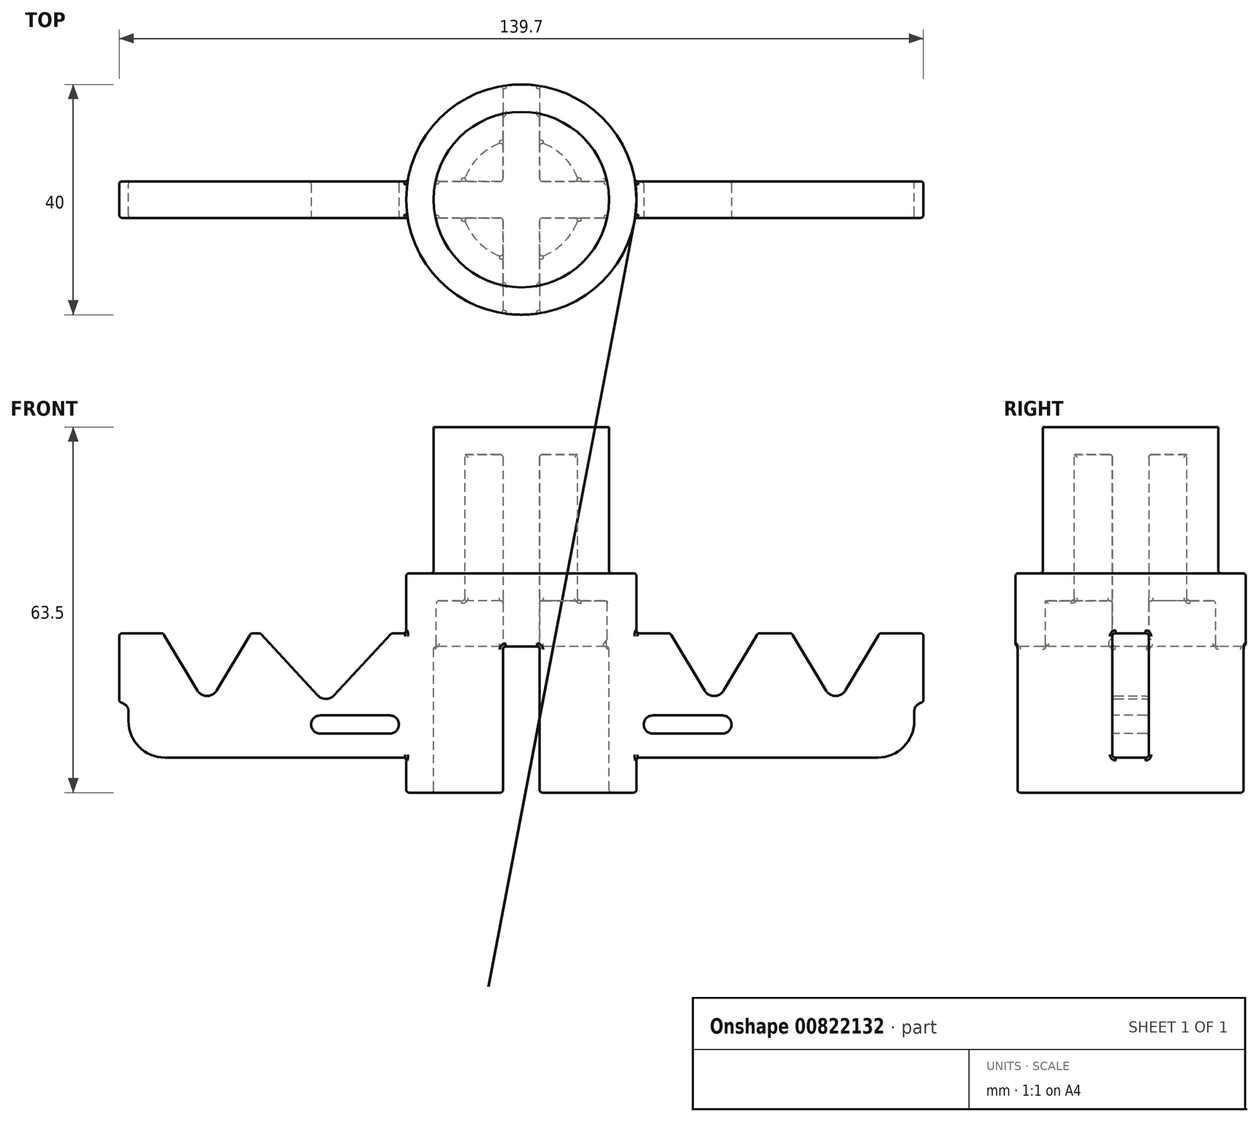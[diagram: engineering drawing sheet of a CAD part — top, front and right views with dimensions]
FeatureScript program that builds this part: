
annotation { "Feature Type Name" : "Feature", "Feature Type Description" : "" }
export const myFeature = defineFeature(function(context is Context, id is Id, definition is map)
    precondition{}
    {
        {
            var Q0;
            Q0=qCreatedBy(makeId("Front.planeOp"),FACE);
            var sketch = newSketch(context, id + "F0", { "sketchPlane" : qUnion([Q0])});
            skLineSegment(sketch, "E0", {"start": v(0, -25.67) * mm, "end": v(61.91, -25.67) * mm});
            skLineSegment(sketch, "E1", {"start": v(69.34, -4.08) * mm, "end": v(62.23, -4.08) * mm});
            skLineSegment(sketch, "E2.trimOffspring", {"start": v(12.23, -4.08) * mm, "end": v(0, -4.08) * mm});
            skLineSegment(sketch, "E3.trimOffspring", {"start": v(47, -4.08) * mm, "end": v(41.1, -4.08) * mm});
            skPoint(sketch, "E4.visualSharp", {"position": v(69.85, -4.08) * mm});
            skArc(sketch, "E4.filletArc", {"start": v(69.85, -4.58) * mm, "mid": v(69.7, -4.22) * mm, "end": v(69.34, -4.08) * mm});
            skPoint(sketch, "E5.visualSharp", {"position": v(69.85, -25.67) * mm});
            skLineSegment(sketch, "E6", {"start": v(0, -46.25) * mm, "end": v(0, -19.99) * mm, "construction": true});
            skLineSegment(sketch, "E7", {"start": v(12.23, -4.08) * mm, "end": v(25.87, -4.08) * mm});
            skLineSegment(sketch, "E8.MirrorCS", {"start": v(0, 38.1) * mm, "end": v(0, 11.84) * mm, "construction": true});
            skArc(sketch, "E9", {"start": v(69.85, -16.1) * mm, "mid": v(68.8, -16.49) * mm, "end": v(68.26, -17.47) * mm});
            skLineSegment(sketch, "E10.trimOffspring", {"start": v(69.85, -16.1) * mm, "end": v(69.85, -4.58) * mm});
            skLineSegment(sketch, "E11", {"start": v(68.26, -17.47) * mm, "end": v(68.26, -19.32) * mm});
            skPoint(sketch, "E12.newPointB", {"position": v(63.5, -25.67) * mm});
            skArc(sketch, "E12.filletArc", {"start": v(61.91, -25.67) * mm, "mid": v(66.4, -23.8) * mm, "end": v(68.26, -19.32) * mm});
            skArc(sketch, "E13.MirrorCS", {"start": v(-69.85, -4.58) * mm, "mid": v(-69.7, -4.22) * mm, "end": v(-69.34, -4.08) * mm});
            skLineSegment(sketch, "E14.MirrorCS", {"start": v(-69.85, -16.1) * mm, "end": v(-69.85, -4.58) * mm});
            skArc(sketch, "E15.MirrorCS", {"start": v(-69.85, -16.1) * mm, "mid": v(-68.8, -16.49) * mm, "end": v(-68.26, -17.47) * mm});
            skLineSegment(sketch, "E16.MirrorCS", {"start": v(-12.23, -4.08) * mm, "end": v(0, -4.08) * mm});
            skLineSegment(sketch, "E17.MirrorCS", {"start": v(-68.26, -17.47) * mm, "end": v(-68.26, -19.32) * mm});
            skLineSegment(sketch, "E18.MirrorCS", {"start": v(-12.23, -4.08) * mm, "end": v(-15.7, -4.08) * mm});
            skLineSegment(sketch, "E19.MirrorCS", {"start": v(-69.34, -4.08) * mm, "end": v(-62.23, -4.08) * mm});
            skLineSegment(sketch, "E20.MirrorCS", {"start": v(0, -25.67) * mm, "end": v(-61.91, -25.67) * mm});
            skPoint(sketch, "E21.MirrorP", {"position": v(-69.85, -4.08) * mm});
            skPoint(sketch, "E22.MirrorP", {"position": v(-69.85, -25.67) * mm});
            skArc(sketch, "E23.MirrorCS", {"start": v(-61.91, -25.67) * mm, "mid": v(-66.4, -23.8) * mm, "end": v(-68.26, -19.32) * mm});
            skPoint(sketch, "E24.MirrorP", {"position": v(-63.5, -25.67) * mm});
            skLineSegment(sketch, "E25", {"start": v(62.23, -4.08) * mm, "end": v(56.24, -14.05) * mm});
            skLineSegment(sketch, "E26", {"start": v(52.98, -14.05) * mm, "end": v(47, -4.08) * mm});
            skLineSegment(sketch, "E27", {"start": v(41.1, -4.08) * mm, "end": v(35.12, -14.05) * mm});
            skLineSegment(sketch, "E28", {"start": v(31.85, -14.05) * mm, "end": v(25.87, -4.08) * mm});
            skLineSegment(sketch, "E29.MirrorCS", {"start": v(-47, -4.08) * mm, "end": v(-45.38, -4.08) * mm});
            skLineSegment(sketch, "E30.MirrorCS", {"start": v(-52.98, -14.05) * mm, "end": v(-47, -4.08) * mm});
            skLineSegment(sketch, "E31.MirrorCS", {"start": v(-62.23, -4.08) * mm, "end": v(-56.24, -14.05) * mm});
            skPoint(sketch, "E32.visualSharp", {"position": v(-54.61, -16.78) * mm});
            skArc(sketch, "E32.filletArc", {"start": v(-56.24, -14.05) * mm, "mid": v(-54.61, -14.98) * mm, "end": v(-52.98, -14.05) * mm});
            skPoint(sketch, "E33.visualSharp", {"position": v(33.49, -16.78) * mm});
            skArc(sketch, "E33.filletArc", {"start": v(31.85, -14.05) * mm, "mid": v(33.49, -14.98) * mm, "end": v(35.12, -14.05) * mm});
            skPoint(sketch, "E34.visualSharp", {"position": v(54.61, -16.78) * mm});
            skArc(sketch, "E34.filletArc", {"start": v(52.98, -14.05) * mm, "mid": v(54.61, -14.98) * mm, "end": v(56.24, -14.05) * mm});
            skPoint(sketch, "E35.endSnap0", {"position": v(-54.61, -14.98) * mm});
            skLineSegment(sketch, "E36", {"start": v(-45.38, -4.08) * mm, "end": v(-35.35, -14.87) * mm});
            skLineSegment(sketch, "E37", {"start": v(-32.56, -14.87) * mm, "end": v(-22.52, -4.08) * mm});
            skLineSegment(sketch, "E38", {"start": v(-15.7, -4.08) * mm, "end": v(-22.52, -4.08) * mm});
            skPoint(sketch, "E39.visualSharp", {"position": v(-33.95, -16.37) * mm});
            skArc(sketch, "E39.filletArc", {"start": v(-35.35, -14.87) * mm, "mid": v(-33.95, -15.48) * mm, "end": v(-32.56, -14.87) * mm});
            skSolve(sketch);
        }
        {
            var Q0;
            Q0 = qSketchRegion(id + "F0", true);
            extrude(context, id + "F1", {"entities" : qUnion([Q0]), "depth" : 3.17 * mm, "offsetDistance" : 25.4 * mm, "hasSecondDirection" : true, "secondDirectionOppositeDirection" : true, "secondDirectionDepth" : 3.17 * mm});
        }
        {
            var Q0;
            Q0=qCreatedBy(makeId("Top.planeOp"),FACE);
            var sketch = newSketch(context, id + "F2", { "sketchPlane" : qUnion([Q0])});
            skCircle(sketch, "E40.0", {"center": v(0, 0) * mm, "radius": 20 * mm});
            skSolve(sketch);
        }
        {
            var Q0;
            Q0=makeQuery(id+"F2.imprint","IMPRINT",FACE,{"disambiguationData":[TD([[makeQuery(id+"F2.imprint","IMPRINT",EDGE,{"derivedFrom":sQuery(id+"F2.wireOp",EDGE,"KXCwf9rt-CnZg-olNI-KTR3-sV1Am3sWeLhQ")}),-1.0]])]});
            var Q1;
            Q1=makeQuery(id+"F2.imprint","IMPRINT",FACE,{"disambiguationData":[TD([[makeQuery(id+"F2.imprint","IMPRINT",EDGE,{"derivedFrom":sQuery(id+"F2.wireOp",EDGE,"E40.0")}),1.0]])]});
            extrude(context, id + "F3", {"entities" : qUnion([Q0, Q1]), "operationType" : NewBodyOperationType.ADD, "oppositeDirection" : true, "depth" : 31.75 * mm, "offsetDistance" : 25.4 * mm, "hasSecondDirection" : true, "secondDirectionOppositeDirection" : false, "secondDirectionDepth" : 31.75 * mm});
        }
        {
            var Q0;
            Q0=makeQuery(id+"F3.opExtrude","CAP_FACE",FACE,{"disambiguationData":[OSD([sQuery(id+"F2.wireOp",EDGE,"E40.0")])],"isStart":false});
            var sketch = newSketch(context, id + "F4", { "sketchPlane" : qUnion([Q0])});
            skCircle(sketch, "E41", {"center": v(0, 0) * mm, "radius": 15.24 * mm});
            skSolve(sketch);
        }
        {
            var Q0;
            Q0=makeQuery(id+"F3.opExtrude","CAP_FACE",FACE,{"disambiguationData":[OSD([sQuery(id+"F2.wireOp",EDGE,"E40.0")])],"isStart":true});
            var sketch = newSketch(context, id + "F5", { "sketchPlane" : qUnion([Q0])});
            skCircle(sketch, "E42", {"center": v(0, 0) * mm, "radius": 15.24 * mm});
            skCircle(sketch, "E43", {"center": v(0, 0) * mm, "radius": 25.4 * mm});
            skSolve(sketch);
        }
        {
            var Q0;
            Q0=makeQuery(id+"F5.imprint","IMPRINT",FACE,{"disambiguationData":[TD([[makeQuery(id+"F5.imprint","IMPRINT",EDGE,{"derivedFrom":sQuery(id+"F5.wireOp",EDGE,"E43")}),1.0]])]});
            var Q1;
            Q1=makeQuery(id+"F5.imprint","IMPRINT",FACE,{"disambiguationData":[TD([[makeQuery(id+"F5.imprint","IMPRINT",EDGE,{"derivedFrom":sQuery(id+"F5.wireOp",EDGE,"E42")}),-1.0]])]});
            extrude(context, id + "F6", {"entities" : qUnion([Q0, Q1]), "operationType" : NewBodyOperationType.REMOVE, "oppositeDirection" : true, "depth" : 25.4 * mm, "offsetDistance" : 25.4 * mm});
        }
        {
            var Q0;
            Q0=makeQuery(id+"F3.opExtrude","CAP_FACE",FACE,{"disambiguationData":[OSD([sQuery(id+"F2.wireOp",EDGE,"E40.0")])],"isStart":false});
            shell(context, id + "F7", {"entities" : qUnion([Q0]), "thickness" : 4.76 * mm});
        }
        {
            var Q0;
            Q0=makeQuery(id+"F4.imprint","IMPRINT",FACE,{"disambiguationData":[TD([[makeQuery(id+"F4.imprint","IMPRINT",EDGE,{"derivedFrom":sQuery(id+"F4.wireOp",EDGE,"E41")}),1.0]])]});
            extrude(context, id + "F8", {"entities" : qUnion([Q0]), "operationType" : NewBodyOperationType.REMOVE, "oppositeDirection" : true, "depth" : 25.4 * mm, "offsetDistance" : 25.4 * mm});
        }
        {
            var Q0;
            Q0=qCreatedBy(makeId("Front.planeOp"),FACE);
            var sketch = newSketch(context, id + "F9", { "sketchPlane" : qUnion([Q0])});
            skLineSegment(sketch, "E44.bottom", {"start": v(3.17, -6.35) * mm, "end": v(-3.18, -6.35) * mm});
            skLineSegment(sketch, "E44.top", {"start": v(3.18, -35.57) * mm, "end": v(-3.17, -35.57) * mm});
            skLineSegment(sketch, "E44.left", {"start": v(3.17, -6.35) * mm, "end": v(3.18, -35.57) * mm});
            skLineSegment(sketch, "E44.right", {"start": v(-3.18, -6.35) * mm, "end": v(-3.17, -35.57) * mm});
            skSolve(sketch);
        }
        {
            var Q0;
            Q0=makeQuery(id+"F9.imprint","IMPRINT",FACE,{"disambiguationData":[TD([[makeQuery(id+"F9.imprint","IMPRINT",EDGE,{"derivedFrom":sQuery(id+"F9.wireOp",EDGE,"E44.bottom")}),1.0]])]});
            extrude(context, id + "F10", {"entities" : qUnion([Q0]), "operationType" : NewBodyOperationType.REMOVE, "endBound" : BoundingType.THROUGH_ALL, "oppositeDirection" : true, "depth" : 25.4 * mm, "offsetDistance" : 25.4 * mm, "hasSecondDirection" : true, "secondDirectionBound" : SecondDirectionBoundingType.THROUGH_ALL, "secondDirectionOppositeDirection" : false, "secondDirectionDepth" : 25.4 * mm});
        }
        {
            var Q0;
            Q0=qCreatedBy(makeId("Top.planeOp"),FACE);
            cPlane(context, id + "F11", {"entities" : qUnion([Q0]), "cplaneType" : CPlaneType.OFFSET, "offset" : 6.35 * mm, "oppositeDirection" : true, "width" : 152.4 * mm, "height" : 152.4 * mm});
        }
        {
            var Q0;
            Q0=qCreatedBy(id+"F11.planeOp",FACE);
            var sketch = newSketch(context, id + "F12", { "sketchPlane" : qUnion([Q0])});
            skLineSegment(sketch, "E45.bottom", {"start": v(18.4, 3.18) * mm, "end": v(-18.44, 3.17) * mm});
            skLineSegment(sketch, "E45.top", {"start": v(18.4, -3.18) * mm, "end": v(-18.44, -3.18) * mm});
            skLineSegment(sketch, "E45.left", {"start": v(18.4, 3.18) * mm, "end": v(18.4, -3.18) * mm});
            skLineSegment(sketch, "E45.right", {"start": v(-18.44, 3.17) * mm, "end": v(-18.44, -3.18) * mm});
            skLineSegment(sketch, "E46.bottom", {"start": v(3.17, 17.5) * mm, "end": v(-3.18, 17.5) * mm});
            skLineSegment(sketch, "E46.top", {"start": v(3.18, -17.88) * mm, "end": v(-3.17, -17.88) * mm});
            skLineSegment(sketch, "E46.left", {"start": v(3.17, 17.5) * mm, "end": v(3.18, -17.88) * mm});
            skLineSegment(sketch, "E46.right", {"start": v(-3.18, 17.5) * mm, "end": v(-3.17, -17.88) * mm});
            skSolve(sketch);
        }
        {
            var Q0;
            {var subQ5=sQuery(id+"F12.wireOp",EDGE,"E46.bottom");Q0=makeQuery(id+"F12.imprint","IMPRINT",FACE,{"disambiguationData":[TD([[makeQuery(id+"F12.imprint","IMPRINT",EDGE,{"derivedFrom":subQ5}),1.0]])]});}
            var Q1;
            {var subQ0=sQuery(id+"F12.wireOp",EDGE,"E45.left");Q1=makeQuery(id+"F12.imprint","IMPRINT",FACE,{"disambiguationData":[TD([[makeQuery(id+"F12.imprint","IMPRINT",EDGE,{"derivedFrom":subQ0}),-1.0]])]});}
            var Q2;
            {var subQ0=sQuery(id+"F12.wireOp",EDGE,"E45.right");Q2=makeQuery(id+"F12.imprint","IMPRINT",FACE,{"disambiguationData":[TD([[makeQuery(id+"F12.imprint","IMPRINT",EDGE,{"derivedFrom":subQ0}),1.0]])]});}
            var Q3;
            {var subQ0=sQuery(id+"F12.wireOp",EDGE,"E46.left");var subQ1=sQuery(id+"F12.wireOp",EDGE,"E45.bottom");var subQ2=makeQuery(id+"F12.imprint","INTERSECT",VERTEX,{"derivedFrom":[subQ1,subQ0]});Q3=makeQuery(id+"F12.imprint","IMPRINT",FACE,{"disambiguationData":[TD([[makeQuery(id+"F12.imprint","IMPRINT",EDGE,{"disambiguationData":[TD([[subQ2,-1.0]])],"derivedFrom":subQ1}),1.0]])]});}
            var Q4;
            {var subQ5=sQuery(id+"F12.wireOp",EDGE,"E46.top");Q4=makeQuery(id+"F12.imprint","IMPRINT",FACE,{"disambiguationData":[TD([[makeQuery(id+"F12.imprint","IMPRINT",EDGE,{"derivedFrom":subQ5}),-1.0]])]});}
            var Q5;
            Q5=makeQuery(id+"F3.opExtrude","CAP_FACE",FACE,{"disambiguationData":[OSD([sQuery(id+"F2.wireOp",EDGE,"E40.0")])],"isStart":true});
            extrude(context, id + "F13", {"entities" : qUnion([Q0, Q1, Q2, Q3, Q4]), "operationType" : NewBodyOperationType.ADD, "endBound" : BoundingType.UP_TO_SURFACE, "depth" : 25.4 * mm, "endBoundEntityFace" : qUnion([Q5]), "offsetDistance" : 25.4 * mm});
        }
        {
            var Q0;
            Q0 = qSketchRegion(id + "F5", true);
            extrude(context, id + "F14", {"entities" : qUnion([Q0]), "operationType" : NewBodyOperationType.REMOVE, "oppositeDirection" : true, "depth" : 25.4 * mm, "offsetDistance" : 25.4 * mm});
        }
        {
            var Q0;
            {var subQ0=sQuery(id+"F0.wireOp",EDGE,"E12.filletArc");var subQ1=sQuery(id+"F0.wireOp",EDGE,"E11");var subQ2=sQuery(id+"F0.wireOp",EDGE,"E10.trimOffspring");var subQ3=sQuery(id+"F0.wireOp",EDGE,"E9");var subQ4=sQuery(id+"F0.wireOp",EDGE,"E25");var subQ5=sQuery(id+"F0.wireOp",EDGE,"E4.filletArc");var subQ6=sQuery(id+"F0.wireOp",EDGE,"E20.MirrorCS");var subQ7=sQuery(id+"F0.wireOp",EDGE,"E0");var subQ8=sQuery(id+"F0.wireOp",EDGE,"E1");var subQ9=sQuery(id+"F0.wireOp",EDGE,"E18.MirrorCS");var subQ10=sQuery(id+"F0.wireOp",EDGE,"E16.MirrorCS");var subQ11=sQuery(id+"F0.wireOp",EDGE,"E7");var subQ12=sQuery(id+"F0.wireOp",EDGE,"E2.trimOffspring");var subQ13=sQuery(id+"F0.wireOp",EDGE,"E3.trimOffspring");var subQ14=sQuery(id+"F0.wireOp",EDGE,"E26");var subQ15=sQuery(id+"F0.wireOp",EDGE,"E27");var subQ16=sQuery(id+"F0.wireOp",EDGE,"E28");Q0=makeQuery(id+"F3.boolean.opBoolean","SPLIT",FACE,{"disambiguationData":[TD([makeQuery(id+"F1.opExtrude","SWEPT_FACE",FACE,{"disambiguationData":[OSD([subQ8])]})])],"derivedFrom":makeQuery(id+"F1.opExtrude","CAP_FACE",FACE,{"disambiguationData":[OSD([subQ7,subQ8,subQ12,subQ13,subQ5,subQ11,subQ3,subQ2,subQ1,subQ0,sQuery(id+"F0.wireOp",EDGE,"E13.MirrorCS"),sQuery(id+"F0.wireOp",EDGE,"E14.MirrorCS"),sQuery(id+"F0.wireOp",EDGE,"E15.MirrorCS"),subQ10,sQuery(id+"F0.wireOp",EDGE,"E17.MirrorCS"),sQuery(id+"F0.wireOp",EDGE,"E19.MirrorCS"),subQ6,sQuery(id+"F0.wireOp",EDGE,"E23.MirrorCS"),subQ4,subQ14,subQ15,subQ16,sQuery(id+"F0.wireOp",EDGE,"E29.MirrorCS"),subQ9,sQuery(id+"F0.wireOp",EDGE,"74dd9322-9861-4298-9e9e-bce7e45bb9e62.MirrorCS"),sQuery(id+"F0.wireOp",EDGE,"74dd9322-9861-4298-9e9e-bce7e45bb9e63.MirrorCS"),sQuery(id+"F0.wireOp",EDGE,"E30.MirrorCS"),sQuery(id+"F0.wireOp",EDGE,"E31.MirrorCS")])],"isStart":false})});}
            var sketch = newSketch(context, id + "F15", { "sketchPlane" : qUnion([Q0])});
            skLineSegment(sketch, "E47.bottom", {"start": v(22.87, -18.34) * mm, "end": v(34.93, -18.34) * mm});
            skLineSegment(sketch, "E47.top", {"start": v(22.87, -21.51) * mm, "end": v(34.93, -21.51) * mm});
            skLineSegment(sketch, "E47.left", {"start": v(21.28, -19.92) * mm, "end": v(21.28, -19.92) * mm});
            skLineSegment(sketch, "E47.right", {"start": v(36.52, -19.92) * mm, "end": v(36.52, -19.92) * mm});
            skPoint(sketch, "E48.visualSharp", {"position": v(21.28, -18.34) * mm});
            skArc(sketch, "E48.filletArc", {"start": v(22.87, -18.34) * mm, "mid": v(21.74, -18.8) * mm, "end": v(21.28, -19.92) * mm});
            skPoint(sketch, "E49.visualSharp", {"position": v(36.52, -18.34) * mm});
            skArc(sketch, "E49.filletArc", {"start": v(36.52, -19.92) * mm, "mid": v(36.05, -18.8) * mm, "end": v(34.93, -18.34) * mm});
            skPoint(sketch, "E50.visualSharp", {"position": v(36.52, -21.51) * mm});
            skArc(sketch, "E50.filletArc", {"start": v(34.93, -21.51) * mm, "mid": v(36.05, -21.05) * mm, "end": v(36.52, -19.92) * mm});
            skPoint(sketch, "E51.visualSharp", {"position": v(21.28, -21.51) * mm});
            skArc(sketch, "E51.filletArc", {"start": v(21.28, -19.92) * mm, "mid": v(21.74, -21.05) * mm, "end": v(22.87, -21.51) * mm});
            skLineSegment(sketch, "E52", {"start": v(0, 0) * mm, "end": v(0, 36.32) * mm, "construction": true});
            skLineSegment(sketch, "E53.MirrorCS", {"start": v(-36.52, -19.92) * mm, "end": v(-36.52, -19.92) * mm});
            skLineSegment(sketch, "E54.MirrorCS", {"start": v(-21.28, -19.92) * mm, "end": v(-21.28, -19.92) * mm});
            skPoint(sketch, "E55.MirrorP", {"position": v(-36.52, -18.34) * mm});
            skPoint(sketch, "E56.MirrorP", {"position": v(-21.28, -21.51) * mm});
            skPoint(sketch, "E57.MirrorP", {"position": v(-21.28, -18.34) * mm});
            skArc(sketch, "E58.MirrorCS", {"start": v(-34.93, -21.51) * mm, "mid": v(-36.05, -21.05) * mm, "end": v(-36.52, -19.92) * mm});
            skArc(sketch, "E59.MirrorCS", {"start": v(-36.52, -19.92) * mm, "mid": v(-36.05, -18.8) * mm, "end": v(-34.93, -18.34) * mm});
            skPoint(sketch, "E60.MirrorP", {"position": v(-36.52, -21.51) * mm});
            skArc(sketch, "E61.MirrorCS", {"start": v(-22.87, -18.34) * mm, "mid": v(-21.74, -18.8) * mm, "end": v(-21.28, -19.92) * mm});
            skArc(sketch, "E62.MirrorCS", {"start": v(-21.28, -19.92) * mm, "mid": v(-21.74, -21.05) * mm, "end": v(-22.87, -21.51) * mm});
            skLineSegment(sketch, "E63", {"start": v(-34.93, -18.34) * mm, "end": v(-22.87, -18.34) * mm});
            skLineSegment(sketch, "E64", {"start": v(-34.93, -21.51) * mm, "end": v(-22.87, -21.51) * mm});
            skSolve(sketch);
        }
        {
            var Q0;
            Q0 = qSketchRegion(id + "F15", true);
            extrude(context, id + "F16", {"entities" : qUnion([Q0]), "operationType" : NewBodyOperationType.REMOVE, "oppositeDirection" : true, "depth" : 25.4 * mm, "offsetDistance" : 25.4 * mm});
        }
        {
            var Q0;
            {var subQ0=sQuery(id+"F2.wireOp",EDGE,"E40.0");Q0=makeQuery(id+"F10.boolean.opBoolean","SPLIT",EDGE,{"disambiguationData":[TD([makeQuery(id+"F10.opExtrude","SWEPT_FACE",FACE,{"disambiguationData":[OSD([sQuery(id+"F9.wireOp",EDGE,"E44.right")])]})])],"derivedFrom":makeQuery(id+"F7.opShell","OFFSET_EDGE",EDGE,{"disambiguationData":[OSD([subQ0])]})});}
            var Q1;
            {var subQ0=sQuery(id+"F12.wireOp",EDGE,"E46.left");Q1=makeQuery(id+"F13.opExtrude","CAP_EDGE",EDGE,{"disambiguationData":[OSD([subQ0]),TDD([makeQuery(id+"F12.imprint","IMPRINT",EDGE,{"disambiguationData":[TD([[makeQuery(id+"F12.imprint","INTERSECT",VERTEX,{"derivedFrom":[sQuery(id+"F12.wireOp",EDGE,"E46.top"),subQ0]}),1.0]])],"derivedFrom":subQ0})])],"isStart":true});}
            var Q2;
            Q2=makeQuery(id+"F10.boolean.opBoolean","INTERSECT",EDGE,{"disambiguationData":[OD(0.0)],"derivedFrom":[makeQuery(id+"F3.opExtrude","SWEPT_FACE",FACE,{"disambiguationData":[OSD([sQuery(id+"F2.wireOp",EDGE,"E40.0")])]}),makeQuery(id+"F10.opExtrude","SWEPT_FACE",FACE,{"disambiguationData":[OSD([sQuery(id+"F9.wireOp",EDGE,"E44.bottom")])]})]});
            var Q3;
            {var subQ0=sQuery(id+"F2.wireOp",EDGE,"E40.0");Q3=makeQuery(id+"F10.boolean.opBoolean","SPLIT",EDGE,{"disambiguationData":[TD([makeQuery(id+"F10.opExtrude","SWEPT_FACE",FACE,{"disambiguationData":[OSD([sQuery(id+"F9.wireOp",EDGE,"E44.left")])]})])],"derivedFrom":makeQuery(id+"F7.opShell","OFFSET_EDGE",EDGE,{"disambiguationData":[OSD([subQ0])]})});}
            var Q4;
            Q4=makeQuery(id+"F10.boolean.opBoolean","INTERSECT",EDGE,{"disambiguationData":[OD(1.0)],"derivedFrom":[makeQuery(id+"F3.opExtrude","SWEPT_FACE",FACE,{"disambiguationData":[OSD([sQuery(id+"F2.wireOp",EDGE,"E40.0")])]}),makeQuery(id+"F10.opExtrude","SWEPT_FACE",FACE,{"disambiguationData":[OSD([sQuery(id+"F9.wireOp",EDGE,"E44.bottom")])]})]});
            var Q5;
            {var subQ0=sQuery(id+"F2.wireOp",EDGE,"E40.0");Q5=makeQuery(id+"F10.boolean.opBoolean","SPLIT",EDGE,{"disambiguationData":[TD([makeQuery(id+"F10.opExtrude","SWEPT_FACE",FACE,{"disambiguationData":[OSD([sQuery(id+"F9.wireOp",EDGE,"E44.right")])]})])],"derivedFrom":makeQuery(id+"F3.opExtrude","CAP_EDGE",EDGE,{"disambiguationData":[OSD([subQ0])],"isStart":false})});}
            var Q6;
            {var subQ0=sQuery(id+"F2.wireOp",EDGE,"E40.0");Q6=makeQuery(id+"F10.boolean.opBoolean","SPLIT",EDGE,{"disambiguationData":[TD([makeQuery(id+"F10.opExtrude","SWEPT_FACE",FACE,{"disambiguationData":[OSD([sQuery(id+"F9.wireOp",EDGE,"E44.left")])]})])],"derivedFrom":makeQuery(id+"F3.opExtrude","CAP_EDGE",EDGE,{"disambiguationData":[OSD([subQ0])],"isStart":false})});}
            var Q7;
            {var subQ0=sQuery(id+"F12.wireOp",EDGE,"E46.left");Q7=makeQuery(id+"F13.opExtrude","CAP_EDGE",EDGE,{"disambiguationData":[OSD([subQ0]),TDD([makeQuery(id+"F12.imprint","IMPRINT",EDGE,{"disambiguationData":[TD([[makeQuery(id+"F12.imprint","INTERSECT",VERTEX,{"derivedFrom":[sQuery(id+"F12.wireOp",EDGE,"E46.bottom"),subQ0]}),-1.0]])],"derivedFrom":subQ0})])],"isStart":true});}
            var Q8;
            Q8=makeQuery(id+"F6.boolean.opBoolean","INTERSECT",EDGE,{"derivedFrom":[makeQuery(id+"F3.opExtrude","SWEPT_FACE",FACE,{"disambiguationData":[OSD([sQuery(id+"F2.wireOp",EDGE,"E40.0")])]}),makeQuery(id+"F6.opExtrude","CAP_FACE",FACE,{"disambiguationData":[OSD([sQuery(id+"F5.wireOp",EDGE,"E42"),sQuery(id+"F5.wireOp",EDGE,"E43")])],"isStart":false})]});
            var Q9;
            {var subQ0=sQuery(id+"F5.wireOp",EDGE,"E42");var subQ1=sQuery(id+"F12.wireOp",EDGE,"E45.right");var subQ2=sQuery(id+"F12.wireOp",EDGE,"E45.top");var subQ8=sQuery(id+"F12.wireOp",EDGE,"E45.left");var subQ9=sQuery(id+"F12.wireOp",EDGE,"E45.bottom");var subQ13=makeQuery(id+"F6.boolean.opBoolean","COPY",EDGE,{"derivedFrom":makeQuery(id+"F6.opExtrude","CAP_EDGE",EDGE,{"disambiguationData":[OSD([subQ0])],"isStart":true})});Q9=makeQuery(id+"F14.boolean.opBoolean","MERGE",EDGE,{"derivedFrom":[makeQuery(id+"F13.boolean.opBoolean","SPLIT",EDGE,{"disambiguationData":[TD([makeQuery(id+"F13.opExtrude","SWEPT_FACE",FACE,{"disambiguationData":[OSD([subQ9]),TDD([makeQuery(id+"F12.imprint","IMPRINT",EDGE,{"disambiguationData":[TD([[makeQuery(id+"F12.imprint","INTERSECT",VERTEX,{"derivedFrom":[subQ9,subQ8]}),-1.0]])],"derivedFrom":subQ9})])]})])],"derivedFrom":subQ13}),makeQuery(id+"F13.boolean.opBoolean","SPLIT",EDGE,{"disambiguationData":[TD([makeQuery(id+"F13.opExtrude","SWEPT_FACE",FACE,{"disambiguationData":[OSD([subQ9]),TDD([makeQuery(id+"F12.imprint","IMPRINT",EDGE,{"disambiguationData":[TD([[makeQuery(id+"F12.imprint","INTERSECT",VERTEX,{"derivedFrom":[subQ9,subQ1]}),1.0]])],"derivedFrom":subQ9})])]})])],"derivedFrom":subQ13}),makeQuery(id+"F13.boolean.opBoolean","SPLIT",EDGE,{"disambiguationData":[TD([makeQuery(id+"F13.opExtrude","SWEPT_FACE",FACE,{"disambiguationData":[OSD([subQ2]),TDD([makeQuery(id+"F12.imprint","IMPRINT",EDGE,{"disambiguationData":[TD([[makeQuery(id+"F12.imprint","INTERSECT",VERTEX,{"derivedFrom":[subQ2,subQ8]}),-1.0]])],"derivedFrom":subQ2})])]})])],"derivedFrom":subQ13}),makeQuery(id+"F13.boolean.opBoolean","SPLIT",EDGE,{"disambiguationData":[TD([makeQuery(id+"F13.opExtrude","SWEPT_FACE",FACE,{"disambiguationData":[OSD([subQ2]),TDD([makeQuery(id+"F12.imprint","IMPRINT",EDGE,{"disambiguationData":[TD([[makeQuery(id+"F12.imprint","INTERSECT",VERTEX,{"derivedFrom":[subQ2,subQ1]}),1.0]])],"derivedFrom":subQ2})])]})])],"derivedFrom":subQ13})],"fromTools":[makeQuery(id+"F14.opExtrude","CAP_EDGE",EDGE,{"disambiguationData":[OSD([subQ0])],"isStart":true})]});}
            var Q10;
            {var subQ0=sQuery(id+"F12.wireOp",EDGE,"E46.right");Q10=makeQuery(id+"F13.opExtrude","CAP_EDGE",EDGE,{"disambiguationData":[OSD([subQ0]),TDD([makeQuery(id+"F12.imprint","IMPRINT",EDGE,{"disambiguationData":[TD([[makeQuery(id+"F12.imprint","INTERSECT",VERTEX,{"derivedFrom":[sQuery(id+"F12.wireOp",EDGE,"E46.bottom"),subQ0]}),-1.0]])],"derivedFrom":subQ0})])],"isStart":true});}
            var Q11;
            Q11=makeQuery(id+"F10.boolean.opBoolean","INTERSECT",EDGE,{"disambiguationData":[OD(0.0)],"derivedFrom":[makeQuery(id+"F3.opExtrude","SWEPT_FACE",FACE,{"disambiguationData":[OSD([sQuery(id+"F2.wireOp",EDGE,"E40.0")])]}),makeQuery(id+"F10.opExtrude","SWEPT_FACE",FACE,{"disambiguationData":[OSD([sQuery(id+"F9.wireOp",EDGE,"E44.right")])]})]});
            var Q12;
            {var subQ0=sQuery(id+"F2.wireOp",EDGE,"E40.0");Q12=makeQuery(id+"F10.boolean.opBoolean","INTERSECT",EDGE,{"disambiguationData":[OD(1.0)],"derivedFrom":[makeQuery(id+"F7.opShell","OFFSET_FACE",FACE,{"disambiguationData":[OSD([subQ0]),TDD([makeQuery(id+"F3.opExtrude","SWEPT_FACE",FACE,{"disambiguationData":[OSD([subQ0])]})])]}),makeQuery(id+"F10.opExtrude","SWEPT_FACE",FACE,{"disambiguationData":[OSD([sQuery(id+"F9.wireOp",EDGE,"E44.left")])]})]});}
            var Q13;
            {var subQ0=sQuery(id+"F5.wireOp",EDGE,"E42");var subQ2=sQuery(id+"F12.wireOp",EDGE,"E45.top");Q13=makeQuery(id+"F13.boolean.opBoolean","SPLIT",EDGE,{"disambiguationData":[TD([makeQuery(id+"F13.opExtrude","SWEPT_FACE",FACE,{"disambiguationData":[OSD([subQ2]),TDD([makeQuery(id+"F12.imprint","IMPRINT",EDGE,{"disambiguationData":[TD([[makeQuery(id+"F12.imprint","INTERSECT",VERTEX,{"derivedFrom":[subQ2,sQuery(id+"F12.wireOp",EDGE,"E45.right")]}),1.0]])],"derivedFrom":subQ2})])]})])],"derivedFrom":makeQuery(id+"F7.opShell","OFFSET_EDGE",EDGE,{"disambiguationData":[OSD([subQ0]),TDD([makeQuery(id+"F6.boolean.opBoolean","COPY",EDGE,{"derivedFrom":makeQuery(id+"F6.opExtrude","CAP_EDGE",EDGE,{"disambiguationData":[OSD([subQ0])],"isStart":false})})])]})});}
            var Q14;
            {var subQ0=sQuery(id+"F12.wireOp",EDGE,"E46.right");var subQ1=sQuery(id+"F2.wireOp",EDGE,"E40.0");Q14=makeQuery(id+"F13.boolean.opBoolean","INTERSECT",EDGE,{"derivedFrom":[makeQuery(id+"F7.opShell","OFFSET_FACE",FACE,{"disambiguationData":[OSD([subQ1]),TDD([makeQuery(id+"F3.opExtrude","SWEPT_FACE",FACE,{"disambiguationData":[OSD([subQ1])]})])]}),makeQuery(id+"F13.opExtrude","SWEPT_FACE",FACE,{"disambiguationData":[OSD([subQ0]),TDD([makeQuery(id+"F12.imprint","IMPRINT",EDGE,{"disambiguationData":[TD([[makeQuery(id+"F12.imprint","INTERSECT",VERTEX,{"derivedFrom":[sQuery(id+"F12.wireOp",EDGE,"E46.top"),subQ0]}),1.0]])],"derivedFrom":subQ0})])]})]});}
            var Q15;
            {var subQ0=sQuery(id+"F12.wireOp",EDGE,"E46.left");var subQ1=sQuery(id+"F2.wireOp",EDGE,"E40.0");Q15=makeQuery(id+"F13.boolean.opBoolean","INTERSECT",EDGE,{"derivedFrom":[makeQuery(id+"F7.opShell","OFFSET_FACE",FACE,{"disambiguationData":[OSD([subQ1]),TDD([makeQuery(id+"F3.opExtrude","SWEPT_FACE",FACE,{"disambiguationData":[OSD([subQ1])]})])]}),makeQuery(id+"F13.opExtrude","SWEPT_FACE",FACE,{"disambiguationData":[OSD([subQ0]),TDD([makeQuery(id+"F12.imprint","IMPRINT",EDGE,{"disambiguationData":[TD([[makeQuery(id+"F12.imprint","INTERSECT",VERTEX,{"derivedFrom":[sQuery(id+"F12.wireOp",EDGE,"E46.top"),subQ0]}),1.0]])],"derivedFrom":subQ0})])]})]});}
            var Q16;
            {var subQ0=sQuery(id+"F12.wireOp",EDGE,"E46.right");var subQ1=sQuery(id+"F2.wireOp",EDGE,"E40.0");Q16=makeQuery(id+"F13.boolean.opBoolean","INTERSECT",EDGE,{"derivedFrom":[makeQuery(id+"F7.opShell","OFFSET_FACE",FACE,{"disambiguationData":[OSD([subQ1]),TDD([makeQuery(id+"F3.opExtrude","SWEPT_FACE",FACE,{"disambiguationData":[OSD([subQ1])]})])]}),makeQuery(id+"F13.opExtrude","SWEPT_FACE",FACE,{"disambiguationData":[OSD([subQ0]),TDD([makeQuery(id+"F12.imprint","IMPRINT",EDGE,{"disambiguationData":[TD([[makeQuery(id+"F12.imprint","INTERSECT",VERTEX,{"derivedFrom":[sQuery(id+"F12.wireOp",EDGE,"E46.bottom"),subQ0]}),-1.0]])],"derivedFrom":subQ0})])]})]});}
            var Q17;
            {var subQ0=sQuery(id+"F12.wireOp",EDGE,"E46.left");var subQ1=sQuery(id+"F2.wireOp",EDGE,"E40.0");Q17=makeQuery(id+"F13.boolean.opBoolean","INTERSECT",EDGE,{"derivedFrom":[makeQuery(id+"F7.opShell","OFFSET_FACE",FACE,{"disambiguationData":[OSD([subQ1]),TDD([makeQuery(id+"F3.opExtrude","SWEPT_FACE",FACE,{"disambiguationData":[OSD([subQ1])]})])]}),makeQuery(id+"F13.opExtrude","SWEPT_FACE",FACE,{"disambiguationData":[OSD([subQ0]),TDD([makeQuery(id+"F12.imprint","IMPRINT",EDGE,{"disambiguationData":[TD([[makeQuery(id+"F12.imprint","INTERSECT",VERTEX,{"derivedFrom":[sQuery(id+"F12.wireOp",EDGE,"E46.bottom"),subQ0]}),-1.0]])],"derivedFrom":subQ0})])]})]});}
            var Q18;
            {var subQ0=sQuery(id+"F2.wireOp",EDGE,"E40.0");Q18=makeQuery(id+"F13.boolean.opBoolean","INTERSECT",EDGE,{"derivedFrom":[makeQuery(id+"F7.opShell","OFFSET_FACE",FACE,{"disambiguationData":[OSD([subQ0]),TDD([makeQuery(id+"F3.opExtrude","SWEPT_FACE",FACE,{"disambiguationData":[OSD([subQ0])]})])]}),makeQuery(id+"F13.opExtrude","CAP_FACE",FACE,{"disambiguationData":[OSD([sQuery(id+"F12.wireOp",EDGE,"E45.bottom"),sQuery(id+"F12.wireOp",EDGE,"E45.top"),sQuery(id+"F12.wireOp",EDGE,"E45.left"),sQuery(id+"F12.wireOp",EDGE,"E45.right"),sQuery(id+"F12.wireOp",EDGE,"E46.bottom"),sQuery(id+"F12.wireOp",EDGE,"E46.top"),sQuery(id+"F12.wireOp",EDGE,"E46.left"),sQuery(id+"F12.wireOp",EDGE,"E46.right")])],"isStart":true})]});}
            var Q19;
            {var subQ0=sQuery(id+"F12.wireOp",EDGE,"E45.bottom");var subQ1=sQuery(id+"F2.wireOp",EDGE,"E40.0");Q19=makeQuery(id+"F13.boolean.opBoolean","INTERSECT",EDGE,{"derivedFrom":[makeQuery(id+"F7.opShell","OFFSET_FACE",FACE,{"disambiguationData":[OSD([subQ1]),TDD([makeQuery(id+"F3.opExtrude","SWEPT_FACE",FACE,{"disambiguationData":[OSD([subQ1])]})])]}),makeQuery(id+"F13.opExtrude","SWEPT_FACE",FACE,{"disambiguationData":[OSD([subQ0]),TDD([makeQuery(id+"F12.imprint","IMPRINT",EDGE,{"disambiguationData":[TD([[makeQuery(id+"F12.imprint","INTERSECT",VERTEX,{"derivedFrom":[subQ0,sQuery(id+"F12.wireOp",EDGE,"E45.right")]}),1.0]])],"derivedFrom":subQ0})])]})]});}
            var Q20;
            {var subQ0=sQuery(id+"F12.wireOp",EDGE,"E45.top");var subQ1=sQuery(id+"F2.wireOp",EDGE,"E40.0");Q20=makeQuery(id+"F13.boolean.opBoolean","INTERSECT",EDGE,{"derivedFrom":[makeQuery(id+"F7.opShell","OFFSET_FACE",FACE,{"disambiguationData":[OSD([subQ1]),TDD([makeQuery(id+"F3.opExtrude","SWEPT_FACE",FACE,{"disambiguationData":[OSD([subQ1])]})])]}),makeQuery(id+"F13.opExtrude","SWEPT_FACE",FACE,{"disambiguationData":[OSD([subQ0]),TDD([makeQuery(id+"F12.imprint","IMPRINT",EDGE,{"disambiguationData":[TD([[makeQuery(id+"F12.imprint","INTERSECT",VERTEX,{"derivedFrom":[subQ0,sQuery(id+"F12.wireOp",EDGE,"E45.right")]}),1.0]])],"derivedFrom":subQ0})])]})]});}
            var Q21;
            Q21=makeQuery(id+"F10.boolean.opBoolean","COPY",EDGE,{"disambiguationData":[OD(0.0)],"derivedFrom":makeQuery(id+"F10.opExtrude","SWEPT_EDGE",EDGE,{"disambiguationData":[OSD([sQuery(id+"F9.wireOp",EDGE,"E44.bottom"),sQuery(id+"F9.wireOp",EDGE,"E44.left")])]})});
            var Q22;
            Q22=makeQuery(id+"F3.boolean.opBoolean","INTERSECT",EDGE,{"disambiguationData":[OD(0.0)],"derivedFrom":[makeQuery(id+"F1.opExtrude","CAP_FACE",FACE,{"disambiguationData":[OSD([sQuery(id+"F0.wireOp",EDGE,"E0"),sQuery(id+"F0.wireOp",EDGE,"E1"),sQuery(id+"F0.wireOp",EDGE,"E2.trimOffspring"),sQuery(id+"F0.wireOp",EDGE,"E3.trimOffspring"),sQuery(id+"F0.wireOp",EDGE,"E4.filletArc"),sQuery(id+"F0.wireOp",EDGE,"E7"),sQuery(id+"F0.wireOp",EDGE,"E9"),sQuery(id+"F0.wireOp",EDGE,"E10.trimOffspring"),sQuery(id+"F0.wireOp",EDGE,"E11"),sQuery(id+"F0.wireOp",EDGE,"E12.filletArc"),sQuery(id+"F0.wireOp",EDGE,"E13.MirrorCS"),sQuery(id+"F0.wireOp",EDGE,"E14.MirrorCS"),sQuery(id+"F0.wireOp",EDGE,"E15.MirrorCS"),sQuery(id+"F0.wireOp",EDGE,"E16.MirrorCS"),sQuery(id+"F0.wireOp",EDGE,"E17.MirrorCS"),sQuery(id+"F0.wireOp",EDGE,"E19.MirrorCS"),sQuery(id+"F0.wireOp",EDGE,"E20.MirrorCS"),sQuery(id+"F0.wireOp",EDGE,"E23.MirrorCS"),sQuery(id+"F0.wireOp",EDGE,"E25"),sQuery(id+"F0.wireOp",EDGE,"E26"),sQuery(id+"F0.wireOp",EDGE,"E27"),sQuery(id+"F0.wireOp",EDGE,"E28"),sQuery(id+"F0.wireOp",EDGE,"E29.MirrorCS"),sQuery(id+"F0.wireOp",EDGE,"E18.MirrorCS"),sQuery(id+"F0.wireOp",EDGE,"E30.MirrorCS"),sQuery(id+"F0.wireOp",EDGE,"E31.MirrorCS"),sQuery(id+"F0.wireOp",EDGE,"E32.filletArc"),sQuery(id+"F0.wireOp",EDGE,"E33.filletArc"),sQuery(id+"F0.wireOp",EDGE,"E34.filletArc"),sQuery(id+"F0.wireOp",EDGE,"E36"),sQuery(id+"F0.wireOp",EDGE,"E37"),sQuery(id+"F0.wireOp",EDGE,"E38"),sQuery(id+"F0.wireOp",EDGE,"E39.filletArc")])],"isStart":false}),makeQuery(id+"F3.opExtrude","SWEPT_FACE",FACE,{"disambiguationData":[OSD([sQuery(id+"F2.wireOp",EDGE,"E40.0")])]})]});
            var Q23;
            {var subQ0=sQuery(id+"F12.wireOp",EDGE,"E45.top");Q23=makeQuery(id+"F13.opExtrude","CAP_EDGE",EDGE,{"disambiguationData":[OSD([subQ0]),TDD([makeQuery(id+"F12.imprint","IMPRINT",EDGE,{"disambiguationData":[TD([[makeQuery(id+"F12.imprint","INTERSECT",VERTEX,{"derivedFrom":[subQ0,sQuery(id+"F12.wireOp",EDGE,"E45.right")]}),1.0]])],"derivedFrom":subQ0})])],"isStart":true});}
            var Q24;
            Q24=makeQuery(id+"F3.boolean.opBoolean","INTERSECT",EDGE,{"disambiguationData":[OD(1.0)],"derivedFrom":[makeQuery(id+"F1.opExtrude","SWEPT_FACE",FACE,{"disambiguationData":[OSD([sQuery(id+"F0.wireOp",EDGE,"E2.trimOffspring"),sQuery(id+"F0.wireOp",EDGE,"E7"),sQuery(id+"F0.wireOp",EDGE,"E16.MirrorCS"),sQuery(id+"F0.wireOp",EDGE,"E18.MirrorCS"),sQuery(id+"F0.wireOp",EDGE,"E38")])]}),makeQuery(id+"F3.opExtrude","SWEPT_FACE",FACE,{"disambiguationData":[OSD([sQuery(id+"F2.wireOp",EDGE,"E40.0")])]})]});
            var Q25;
            {var subQ0=sQuery(id+"F5.wireOp",EDGE,"E42");var subQ2=sQuery(id+"F12.wireOp",EDGE,"E45.top");Q25=makeQuery(id+"F13.boolean.opBoolean","SPLIT",EDGE,{"disambiguationData":[TD([makeQuery(id+"F13.opExtrude","SWEPT_FACE",FACE,{"disambiguationData":[OSD([subQ2]),TDD([makeQuery(id+"F12.imprint","IMPRINT",EDGE,{"disambiguationData":[TD([[makeQuery(id+"F12.imprint","INTERSECT",VERTEX,{"derivedFrom":[subQ2,sQuery(id+"F12.wireOp",EDGE,"E45.left")]}),-1.0]])],"derivedFrom":subQ2})])]})])],"derivedFrom":makeQuery(id+"F7.opShell","OFFSET_EDGE",EDGE,{"disambiguationData":[OSD([subQ0]),TDD([makeQuery(id+"F6.boolean.opBoolean","COPY",EDGE,{"derivedFrom":makeQuery(id+"F6.opExtrude","CAP_EDGE",EDGE,{"disambiguationData":[OSD([subQ0])],"isStart":true})})])]})});}
            var Q26;
            {var subQ0=sQuery(id+"F12.wireOp",EDGE,"E45.top");Q26=makeQuery(id+"F13.boolean.opBoolean","INTERSECT",EDGE,{"derivedFrom":[makeQuery(id+"F7.opShell","OFFSET_FACE",FACE,{"disambiguationData":[OSD([sQuery(id+"F5.wireOp",EDGE,"E42"),sQuery(id+"F5.wireOp",EDGE,"E43")])]}),makeQuery(id+"F13.opExtrude","SWEPT_FACE",FACE,{"disambiguationData":[OSD([subQ0]),TDD([makeQuery(id+"F12.imprint","IMPRINT",EDGE,{"disambiguationData":[TD([[makeQuery(id+"F12.imprint","INTERSECT",VERTEX,{"derivedFrom":[subQ0,sQuery(id+"F12.wireOp",EDGE,"E45.right")]}),1.0]])],"derivedFrom":subQ0})])]})]});}
            var Q27;
            Q27=makeQuery(id+"F1.opExtrude","CAP_EDGE",EDGE,{"disambiguationData":[OSD([sQuery(id+"F0.wireOp",EDGE,"E4.filletArc")])],"isStart":false});
            var Q28;
            {var subQ0=sQuery(id+"F5.wireOp",EDGE,"E42");var subQ5=sQuery(id+"F12.wireOp",EDGE,"E45.top");var subQ7=sQuery(id+"F12.wireOp",EDGE,"E45.right");var subQ8=makeQuery(id+"F6.boolean.opBoolean","COPY",EDGE,{"derivedFrom":makeQuery(id+"F6.opExtrude","CAP_EDGE",EDGE,{"disambiguationData":[OSD([subQ0])],"isStart":false})});var subQ9=sQuery(id+"F12.wireOp",EDGE,"E45.left");var subQ13=sQuery(id+"F12.wireOp",EDGE,"E45.bottom");Q28=makeQuery(id+"F14.boolean.opBoolean","MERGE",EDGE,{"derivedFrom":[makeQuery(id+"F13.boolean.opBoolean","SPLIT",EDGE,{"disambiguationData":[TD([makeQuery(id+"F13.opExtrude","SWEPT_FACE",FACE,{"disambiguationData":[OSD([subQ13]),TDD([makeQuery(id+"F12.imprint","IMPRINT",EDGE,{"disambiguationData":[TD([[makeQuery(id+"F12.imprint","INTERSECT",VERTEX,{"derivedFrom":[subQ13,subQ9]}),-1.0]])],"derivedFrom":subQ13})])]})])],"derivedFrom":subQ8}),makeQuery(id+"F13.boolean.opBoolean","SPLIT",EDGE,{"disambiguationData":[TD([makeQuery(id+"F13.opExtrude","SWEPT_FACE",FACE,{"disambiguationData":[OSD([subQ13]),TDD([makeQuery(id+"F12.imprint","IMPRINT",EDGE,{"disambiguationData":[TD([[makeQuery(id+"F12.imprint","INTERSECT",VERTEX,{"derivedFrom":[subQ13,subQ7]}),1.0]])],"derivedFrom":subQ13})])]})])],"derivedFrom":subQ8}),makeQuery(id+"F13.boolean.opBoolean","SPLIT",EDGE,{"disambiguationData":[TD([makeQuery(id+"F13.opExtrude","SWEPT_FACE",FACE,{"disambiguationData":[OSD([subQ5]),TDD([makeQuery(id+"F12.imprint","IMPRINT",EDGE,{"disambiguationData":[TD([[makeQuery(id+"F12.imprint","INTERSECT",VERTEX,{"derivedFrom":[subQ5,subQ9]}),-1.0]])],"derivedFrom":subQ5})])]})])],"derivedFrom":subQ8}),makeQuery(id+"F13.boolean.opBoolean","SPLIT",EDGE,{"disambiguationData":[TD([makeQuery(id+"F13.opExtrude","SWEPT_FACE",FACE,{"disambiguationData":[OSD([subQ5]),TDD([makeQuery(id+"F12.imprint","IMPRINT",EDGE,{"disambiguationData":[TD([[makeQuery(id+"F12.imprint","INTERSECT",VERTEX,{"derivedFrom":[subQ5,subQ7]}),1.0]])],"derivedFrom":subQ5})])]})])],"derivedFrom":subQ8})],"fromTools":[makeQuery(id+"F14.opExtrude","CAP_EDGE",EDGE,{"disambiguationData":[OSD([subQ0])],"isStart":false})]});}
            var Q29;
            Q29=makeQuery(id+"F1.opExtrude","SWEPT_EDGE",EDGE,{"disambiguationData":[OSD([sQuery(id+"F0.wireOp",EDGE,"E9"),sQuery(id+"F0.wireOp",EDGE,"E10.trimOffspring")])]});
            var Q30;
            Q30=makeQuery(id+"F1.opExtrude","SWEPT_EDGE",EDGE,{"disambiguationData":[OSD([sQuery(id+"F0.wireOp",EDGE,"E9"),sQuery(id+"F0.wireOp",EDGE,"E11")])]});
            var Q31;
            Q31=makeQuery(id+"F1.opExtrude","SWEPT_EDGE",EDGE,{"disambiguationData":[OSD([sQuery(id+"F0.wireOp",EDGE,"E1"),sQuery(id+"F0.wireOp",EDGE,"E4.filletArc")])]});
            var Q32;
            Q32=makeQuery(id+"F1.opExtrude","SWEPT_EDGE",EDGE,{"disambiguationData":[OSD([sQuery(id+"F0.wireOp",EDGE,"E4.filletArc"),sQuery(id+"F0.wireOp",EDGE,"E10.trimOffspring")])]});
            var Q33;
            Q33=makeQuery(id+"F10.boolean.opBoolean","INTERSECT",EDGE,{"disambiguationData":[OD(0.0)],"derivedFrom":[makeQuery(id+"F3.opExtrude","CAP_FACE",FACE,{"disambiguationData":[OSD([sQuery(id+"F2.wireOp",EDGE,"E40.0")])],"isStart":false}),makeQuery(id+"F10.opExtrude","SWEPT_FACE",FACE,{"disambiguationData":[OSD([sQuery(id+"F9.wireOp",EDGE,"E44.right")])]})]});
            var Q34;
            {var subQ0=sQuery(id+"F12.wireOp",EDGE,"E45.top");Q34=makeQuery(id+"F13.boolean.opBoolean","INTERSECT",EDGE,{"derivedFrom":[makeQuery(id+"F7.opShell","OFFSET_FACE",FACE,{"disambiguationData":[OSD([sQuery(id+"F5.wireOp",EDGE,"E42"),sQuery(id+"F5.wireOp",EDGE,"E43")])]}),makeQuery(id+"F13.opExtrude","SWEPT_FACE",FACE,{"disambiguationData":[OSD([subQ0]),TDD([makeQuery(id+"F12.imprint","IMPRINT",EDGE,{"disambiguationData":[TD([[makeQuery(id+"F12.imprint","INTERSECT",VERTEX,{"derivedFrom":[subQ0,sQuery(id+"F12.wireOp",EDGE,"E45.left")]}),-1.0]])],"derivedFrom":subQ0})])]})]});}
            var Q35;
            Q35=makeQuery(id+"F13.opExtrude","SWEPT_EDGE",EDGE,{"disambiguationData":[OSD([sQuery(id+"F12.wireOp",EDGE,"E45.bottom"),sQuery(id+"F12.wireOp",EDGE,"E46.left")])]});
            var Q36;
            {var subQ0=sQuery(id+"F5.wireOp",EDGE,"E42");var subQ2=sQuery(id+"F12.wireOp",EDGE,"E45.top");Q36=makeQuery(id+"F13.boolean.opBoolean","SPLIT",EDGE,{"disambiguationData":[TD([makeQuery(id+"F13.opExtrude","SWEPT_FACE",FACE,{"disambiguationData":[OSD([subQ2]),TDD([makeQuery(id+"F12.imprint","IMPRINT",EDGE,{"disambiguationData":[TD([[makeQuery(id+"F12.imprint","INTERSECT",VERTEX,{"derivedFrom":[subQ2,sQuery(id+"F12.wireOp",EDGE,"E45.right")]}),1.0]])],"derivedFrom":subQ2})])]})])],"derivedFrom":makeQuery(id+"F7.opShell","OFFSET_EDGE",EDGE,{"disambiguationData":[OSD([subQ0]),TDD([makeQuery(id+"F6.boolean.opBoolean","COPY",EDGE,{"derivedFrom":makeQuery(id+"F6.opExtrude","CAP_EDGE",EDGE,{"disambiguationData":[OSD([subQ0])],"isStart":true})})])]})});}
            var Q37;
            {var subQ0=sQuery(id+"F12.wireOp",EDGE,"E45.bottom");Q37=makeQuery(id+"F13.opExtrude","CAP_EDGE",EDGE,{"disambiguationData":[OSD([subQ0]),TDD([makeQuery(id+"F12.imprint","IMPRINT",EDGE,{"disambiguationData":[TD([[makeQuery(id+"F12.imprint","INTERSECT",VERTEX,{"derivedFrom":[subQ0,sQuery(id+"F12.wireOp",EDGE,"E45.left")]}),-1.0]])],"derivedFrom":subQ0})])],"isStart":true});}
            var Q38;
            {var subQ0=sQuery(id+"F2.wireOp",EDGE,"E40.0");Q38=makeQuery(id+"F10.boolean.opBoolean","INTERSECT",EDGE,{"disambiguationData":[OD(0.0)],"derivedFrom":[makeQuery(id+"F7.opShell","OFFSET_FACE",FACE,{"disambiguationData":[OSD([subQ0]),TDD([makeQuery(id+"F3.opExtrude","SWEPT_FACE",FACE,{"disambiguationData":[OSD([subQ0])]})])]}),makeQuery(id+"F10.opExtrude","SWEPT_FACE",FACE,{"disambiguationData":[OSD([sQuery(id+"F9.wireOp",EDGE,"E44.right")])]})]});}
            var Q39;
            {var subQ0=sQuery(id+"F12.wireOp",EDGE,"E45.top");Q39=makeQuery(id+"F13.opExtrude","CAP_EDGE",EDGE,{"disambiguationData":[OSD([subQ0]),TDD([makeQuery(id+"F12.imprint","IMPRINT",EDGE,{"disambiguationData":[TD([[makeQuery(id+"F12.imprint","INTERSECT",VERTEX,{"derivedFrom":[subQ0,sQuery(id+"F12.wireOp",EDGE,"E45.left")]}),-1.0]])],"derivedFrom":subQ0})])],"isStart":true});}
            var Q40;
            Q40=makeQuery(id+"F10.boolean.opBoolean","INTERSECT",EDGE,{"disambiguationData":[OD(1.0)],"derivedFrom":[makeQuery(id+"F3.opExtrude","SWEPT_FACE",FACE,{"disambiguationData":[OSD([sQuery(id+"F2.wireOp",EDGE,"E40.0")])]}),makeQuery(id+"F10.opExtrude","SWEPT_FACE",FACE,{"disambiguationData":[OSD([sQuery(id+"F9.wireOp",EDGE,"E44.left")])]})]});
            var Q41;
            Q41=makeQuery(id+"F10.boolean.opBoolean","INTERSECT",EDGE,{"disambiguationData":[OD(1.0)],"derivedFrom":[makeQuery(id+"F3.opExtrude","CAP_FACE",FACE,{"disambiguationData":[OSD([sQuery(id+"F2.wireOp",EDGE,"E40.0")])],"isStart":false}),makeQuery(id+"F10.opExtrude","SWEPT_FACE",FACE,{"disambiguationData":[OSD([sQuery(id+"F9.wireOp",EDGE,"E44.left")])]})]});
            var Q42;
            Q42=makeQuery(id+"F10.boolean.opBoolean","COPY",EDGE,{"disambiguationData":[OD(1.0)],"derivedFrom":makeQuery(id+"F10.opExtrude","SWEPT_EDGE",EDGE,{"disambiguationData":[OSD([sQuery(id+"F9.wireOp",EDGE,"E44.bottom"),sQuery(id+"F9.wireOp",EDGE,"E44.left")])]})});
            var Q43;
            Q43=makeQuery(id+"F10.boolean.opBoolean","COPY",EDGE,{"disambiguationData":[OD(1.0)],"derivedFrom":makeQuery(id+"F10.opExtrude","SWEPT_EDGE",EDGE,{"disambiguationData":[OSD([sQuery(id+"F9.wireOp",EDGE,"E44.bottom"),sQuery(id+"F9.wireOp",EDGE,"E44.right")])]})});
            var Q44;
            Q44=makeQuery(id+"F3.boolean.opBoolean","INTERSECT",EDGE,{"disambiguationData":[OD(1.0)],"derivedFrom":[makeQuery(id+"F1.opExtrude","CAP_FACE",FACE,{"disambiguationData":[OSD([sQuery(id+"F0.wireOp",EDGE,"E0"),sQuery(id+"F0.wireOp",EDGE,"E1"),sQuery(id+"F0.wireOp",EDGE,"E2.trimOffspring"),sQuery(id+"F0.wireOp",EDGE,"E3.trimOffspring"),sQuery(id+"F0.wireOp",EDGE,"E4.filletArc"),sQuery(id+"F0.wireOp",EDGE,"E7"),sQuery(id+"F0.wireOp",EDGE,"E9"),sQuery(id+"F0.wireOp",EDGE,"E10.trimOffspring"),sQuery(id+"F0.wireOp",EDGE,"E11"),sQuery(id+"F0.wireOp",EDGE,"E12.filletArc"),sQuery(id+"F0.wireOp",EDGE,"E13.MirrorCS"),sQuery(id+"F0.wireOp",EDGE,"E14.MirrorCS"),sQuery(id+"F0.wireOp",EDGE,"E15.MirrorCS"),sQuery(id+"F0.wireOp",EDGE,"E16.MirrorCS"),sQuery(id+"F0.wireOp",EDGE,"E17.MirrorCS"),sQuery(id+"F0.wireOp",EDGE,"E19.MirrorCS"),sQuery(id+"F0.wireOp",EDGE,"E20.MirrorCS"),sQuery(id+"F0.wireOp",EDGE,"E23.MirrorCS"),sQuery(id+"F0.wireOp",EDGE,"E25"),sQuery(id+"F0.wireOp",EDGE,"E26"),sQuery(id+"F0.wireOp",EDGE,"E27"),sQuery(id+"F0.wireOp",EDGE,"E28"),sQuery(id+"F0.wireOp",EDGE,"E29.MirrorCS"),sQuery(id+"F0.wireOp",EDGE,"E18.MirrorCS"),sQuery(id+"F0.wireOp",EDGE,"E30.MirrorCS"),sQuery(id+"F0.wireOp",EDGE,"E31.MirrorCS"),sQuery(id+"F0.wireOp",EDGE,"E32.filletArc"),sQuery(id+"F0.wireOp",EDGE,"E33.filletArc"),sQuery(id+"F0.wireOp",EDGE,"E34.filletArc"),sQuery(id+"F0.wireOp",EDGE,"E36"),sQuery(id+"F0.wireOp",EDGE,"E37"),sQuery(id+"F0.wireOp",EDGE,"E38"),sQuery(id+"F0.wireOp",EDGE,"E39.filletArc")])],"isStart":false}),makeQuery(id+"F3.opExtrude","SWEPT_FACE",FACE,{"disambiguationData":[OSD([sQuery(id+"F2.wireOp",EDGE,"E40.0")])]})]});
            var Q45;
            Q45=makeQuery(id+"F3.boolean.opBoolean","INTERSECT",EDGE,{"disambiguationData":[OD(0.0)],"derivedFrom":[makeQuery(id+"F1.opExtrude","SWEPT_FACE",FACE,{"disambiguationData":[OSD([sQuery(id+"F0.wireOp",EDGE,"E0"),sQuery(id+"F0.wireOp",EDGE,"E20.MirrorCS")])]}),makeQuery(id+"F3.opExtrude","SWEPT_FACE",FACE,{"disambiguationData":[OSD([sQuery(id+"F2.wireOp",EDGE,"E40.0")])]})]});
            var Q46;
            Q46=makeQuery(id+"F3.boolean.opBoolean","INTERSECT",EDGE,{"disambiguationData":[OD(1.0)],"derivedFrom":[makeQuery(id+"F1.opExtrude","SWEPT_FACE",FACE,{"disambiguationData":[OSD([sQuery(id+"F0.wireOp",EDGE,"E0"),sQuery(id+"F0.wireOp",EDGE,"E20.MirrorCS")])]}),makeQuery(id+"F3.opExtrude","SWEPT_FACE",FACE,{"disambiguationData":[OSD([sQuery(id+"F2.wireOp",EDGE,"E40.0")])]})]});
            var Q47;
            Q47=makeQuery(id+"F10.boolean.opBoolean","INTERSECT",EDGE,{"disambiguationData":[OD(0.0)],"derivedFrom":[makeQuery(id+"F3.opExtrude","CAP_FACE",FACE,{"disambiguationData":[OSD([sQuery(id+"F2.wireOp",EDGE,"E40.0")])],"isStart":false}),makeQuery(id+"F10.opExtrude","SWEPT_FACE",FACE,{"disambiguationData":[OSD([sQuery(id+"F9.wireOp",EDGE,"E44.left")])]})]});
            var Q48;
            {var subQ0=sQuery(id+"F2.wireOp",EDGE,"E40.0");Q48=makeQuery(id+"F10.boolean.opBoolean","INTERSECT",EDGE,{"disambiguationData":[OD(0.0)],"derivedFrom":[makeQuery(id+"F7.opShell","OFFSET_FACE",FACE,{"disambiguationData":[OSD([subQ0]),TDD([makeQuery(id+"F3.opExtrude","SWEPT_FACE",FACE,{"disambiguationData":[OSD([subQ0])]})])]}),makeQuery(id+"F10.opExtrude","SWEPT_FACE",FACE,{"disambiguationData":[OSD([sQuery(id+"F9.wireOp",EDGE,"E44.left")])]})]});}
            var Q49;
            Q49=makeQuery(id+"F10.boolean.opBoolean","INTERSECT",EDGE,{"disambiguationData":[OD(1.0)],"derivedFrom":[makeQuery(id+"F3.opExtrude","CAP_FACE",FACE,{"disambiguationData":[OSD([sQuery(id+"F2.wireOp",EDGE,"E40.0")])],"isStart":false}),makeQuery(id+"F10.opExtrude","SWEPT_FACE",FACE,{"disambiguationData":[OSD([sQuery(id+"F9.wireOp",EDGE,"E44.right")])]})]});
            var Q50;
            Q50=makeQuery(id+"F10.boolean.opBoolean","COPY",EDGE,{"disambiguationData":[OD(0.0)],"derivedFrom":makeQuery(id+"F10.opExtrude","SWEPT_EDGE",EDGE,{"disambiguationData":[OSD([sQuery(id+"F9.wireOp",EDGE,"E44.bottom"),sQuery(id+"F9.wireOp",EDGE,"E44.right")])]})});
            var Q51;
            Q51=makeQuery(id+"F3.boolean.opBoolean","INTERSECT",EDGE,{"disambiguationData":[OD(1.0)],"derivedFrom":[makeQuery(id+"F1.opExtrude","CAP_FACE",FACE,{"disambiguationData":[OSD([sQuery(id+"F0.wireOp",EDGE,"E0"),sQuery(id+"F0.wireOp",EDGE,"E1"),sQuery(id+"F0.wireOp",EDGE,"E2.trimOffspring"),sQuery(id+"F0.wireOp",EDGE,"E3.trimOffspring"),sQuery(id+"F0.wireOp",EDGE,"E4.filletArc"),sQuery(id+"F0.wireOp",EDGE,"E7"),sQuery(id+"F0.wireOp",EDGE,"E9"),sQuery(id+"F0.wireOp",EDGE,"E10.trimOffspring"),sQuery(id+"F0.wireOp",EDGE,"E11"),sQuery(id+"F0.wireOp",EDGE,"E12.filletArc"),sQuery(id+"F0.wireOp",EDGE,"E13.MirrorCS"),sQuery(id+"F0.wireOp",EDGE,"E14.MirrorCS"),sQuery(id+"F0.wireOp",EDGE,"E15.MirrorCS"),sQuery(id+"F0.wireOp",EDGE,"E16.MirrorCS"),sQuery(id+"F0.wireOp",EDGE,"E17.MirrorCS"),sQuery(id+"F0.wireOp",EDGE,"E19.MirrorCS"),sQuery(id+"F0.wireOp",EDGE,"E20.MirrorCS"),sQuery(id+"F0.wireOp",EDGE,"E23.MirrorCS"),sQuery(id+"F0.wireOp",EDGE,"E25"),sQuery(id+"F0.wireOp",EDGE,"E26"),sQuery(id+"F0.wireOp",EDGE,"E27"),sQuery(id+"F0.wireOp",EDGE,"E28"),sQuery(id+"F0.wireOp",EDGE,"E29.MirrorCS"),sQuery(id+"F0.wireOp",EDGE,"E18.MirrorCS"),sQuery(id+"F0.wireOp",EDGE,"E30.MirrorCS"),sQuery(id+"F0.wireOp",EDGE,"E31.MirrorCS"),sQuery(id+"F0.wireOp",EDGE,"E32.filletArc"),sQuery(id+"F0.wireOp",EDGE,"E33.filletArc"),sQuery(id+"F0.wireOp",EDGE,"E34.filletArc"),sQuery(id+"F0.wireOp",EDGE,"E36"),sQuery(id+"F0.wireOp",EDGE,"E37"),sQuery(id+"F0.wireOp",EDGE,"E38"),sQuery(id+"F0.wireOp",EDGE,"E39.filletArc")])],"isStart":true}),makeQuery(id+"F3.opExtrude","SWEPT_FACE",FACE,{"disambiguationData":[OSD([sQuery(id+"F2.wireOp",EDGE,"E40.0")])]})]});
            var Q52;
            Q52=makeQuery(id+"F3.boolean.opBoolean","INTERSECT",EDGE,{"disambiguationData":[OD(0.0)],"derivedFrom":[makeQuery(id+"F1.opExtrude","SWEPT_FACE",FACE,{"disambiguationData":[OSD([sQuery(id+"F0.wireOp",EDGE,"E2.trimOffspring"),sQuery(id+"F0.wireOp",EDGE,"E7"),sQuery(id+"F0.wireOp",EDGE,"E16.MirrorCS"),sQuery(id+"F0.wireOp",EDGE,"E18.MirrorCS"),sQuery(id+"F0.wireOp",EDGE,"E38")])]}),makeQuery(id+"F3.opExtrude","SWEPT_FACE",FACE,{"disambiguationData":[OSD([sQuery(id+"F2.wireOp",EDGE,"E40.0")])]})]});
            var Q53;
            Q53=makeQuery(id+"F3.boolean.opBoolean","INTERSECT",EDGE,{"disambiguationData":[OD(0.0)],"derivedFrom":[makeQuery(id+"F1.opExtrude","CAP_FACE",FACE,{"disambiguationData":[OSD([sQuery(id+"F0.wireOp",EDGE,"E0"),sQuery(id+"F0.wireOp",EDGE,"E1"),sQuery(id+"F0.wireOp",EDGE,"E2.trimOffspring"),sQuery(id+"F0.wireOp",EDGE,"E3.trimOffspring"),sQuery(id+"F0.wireOp",EDGE,"E4.filletArc"),sQuery(id+"F0.wireOp",EDGE,"E7"),sQuery(id+"F0.wireOp",EDGE,"E9"),sQuery(id+"F0.wireOp",EDGE,"E10.trimOffspring"),sQuery(id+"F0.wireOp",EDGE,"E11"),sQuery(id+"F0.wireOp",EDGE,"E12.filletArc"),sQuery(id+"F0.wireOp",EDGE,"E13.MirrorCS"),sQuery(id+"F0.wireOp",EDGE,"E14.MirrorCS"),sQuery(id+"F0.wireOp",EDGE,"E15.MirrorCS"),sQuery(id+"F0.wireOp",EDGE,"E16.MirrorCS"),sQuery(id+"F0.wireOp",EDGE,"E17.MirrorCS"),sQuery(id+"F0.wireOp",EDGE,"E19.MirrorCS"),sQuery(id+"F0.wireOp",EDGE,"E20.MirrorCS"),sQuery(id+"F0.wireOp",EDGE,"E23.MirrorCS"),sQuery(id+"F0.wireOp",EDGE,"E25"),sQuery(id+"F0.wireOp",EDGE,"E26"),sQuery(id+"F0.wireOp",EDGE,"E27"),sQuery(id+"F0.wireOp",EDGE,"E28"),sQuery(id+"F0.wireOp",EDGE,"E29.MirrorCS"),sQuery(id+"F0.wireOp",EDGE,"E18.MirrorCS"),sQuery(id+"F0.wireOp",EDGE,"E30.MirrorCS"),sQuery(id+"F0.wireOp",EDGE,"E31.MirrorCS"),sQuery(id+"F0.wireOp",EDGE,"E32.filletArc"),sQuery(id+"F0.wireOp",EDGE,"E33.filletArc"),sQuery(id+"F0.wireOp",EDGE,"E34.filletArc"),sQuery(id+"F0.wireOp",EDGE,"E36"),sQuery(id+"F0.wireOp",EDGE,"E37"),sQuery(id+"F0.wireOp",EDGE,"E38"),sQuery(id+"F0.wireOp",EDGE,"E39.filletArc")])],"isStart":true}),makeQuery(id+"F3.opExtrude","SWEPT_FACE",FACE,{"disambiguationData":[OSD([sQuery(id+"F2.wireOp",EDGE,"E40.0")])]})]});
            var Q54;
            Q54=makeQuery(id+"F1.opExtrude","SWEPT_EDGE",EDGE,{"disambiguationData":[OSD([sQuery(id+"F0.wireOp",EDGE,"E0"),sQuery(id+"F0.wireOp",EDGE,"E12.filletArc")])]});
            var Q55;
            {var subQ0=sQuery(id+"F12.wireOp",EDGE,"E46.left");Q55=makeQuery(id+"F13.boolean.opBoolean","INTERSECT",EDGE,{"derivedFrom":[makeQuery(id+"F7.opShell","OFFSET_FACE",FACE,{"disambiguationData":[OSD([sQuery(id+"F5.wireOp",EDGE,"E42")])]}),makeQuery(id+"F13.opExtrude","SWEPT_FACE",FACE,{"disambiguationData":[OSD([subQ0]),TDD([makeQuery(id+"F12.imprint","IMPRINT",EDGE,{"disambiguationData":[TD([[makeQuery(id+"F12.imprint","INTERSECT",VERTEX,{"derivedFrom":[sQuery(id+"F12.wireOp",EDGE,"E46.bottom"),subQ0]}),-1.0]])],"derivedFrom":subQ0})])]})]});}
            var Q56;
            {var subQ0=sQuery(id+"F12.wireOp",EDGE,"E46.right");Q56=makeQuery(id+"F13.opExtrude","CAP_EDGE",EDGE,{"disambiguationData":[OSD([subQ0]),TDD([makeQuery(id+"F12.imprint","IMPRINT",EDGE,{"disambiguationData":[TD([[makeQuery(id+"F12.imprint","INTERSECT",VERTEX,{"derivedFrom":[sQuery(id+"F12.wireOp",EDGE,"E46.top"),subQ0]}),1.0]])],"derivedFrom":subQ0})])],"isStart":true});}
            var Q57;
            {var subQ0=sQuery(id+"F2.wireOp",EDGE,"E40.0");Q57=makeQuery(id+"F10.boolean.opBoolean","INTERSECT",EDGE,{"disambiguationData":[OD(1.0)],"derivedFrom":[makeQuery(id+"F7.opShell","OFFSET_FACE",FACE,{"disambiguationData":[OSD([subQ0]),TDD([makeQuery(id+"F3.opExtrude","SWEPT_FACE",FACE,{"disambiguationData":[OSD([subQ0])]})])]}),makeQuery(id+"F10.opExtrude","SWEPT_FACE",FACE,{"disambiguationData":[OSD([sQuery(id+"F9.wireOp",EDGE,"E44.right")])]})]});}
            var Q58;
            {var subQ0=sQuery(id+"F12.wireOp",EDGE,"E45.bottom");Q58=makeQuery(id+"F13.opExtrude","CAP_EDGE",EDGE,{"disambiguationData":[OSD([subQ0]),TDD([makeQuery(id+"F12.imprint","IMPRINT",EDGE,{"disambiguationData":[TD([[makeQuery(id+"F12.imprint","INTERSECT",VERTEX,{"derivedFrom":[subQ0,sQuery(id+"F12.wireOp",EDGE,"E45.right")]}),1.0]])],"derivedFrom":subQ0})])],"isStart":true});}
            var Q59;
            Q59=makeQuery(id+"F10.boolean.opBoolean","INTERSECT",EDGE,{"disambiguationData":[OD(1.0)],"derivedFrom":[makeQuery(id+"F3.opExtrude","SWEPT_FACE",FACE,{"disambiguationData":[OSD([sQuery(id+"F2.wireOp",EDGE,"E40.0")])]}),makeQuery(id+"F10.opExtrude","SWEPT_FACE",FACE,{"disambiguationData":[OSD([sQuery(id+"F9.wireOp",EDGE,"E44.right")])]})]});
            var Q60;
            Q60=makeQuery(id+"F10.boolean.opBoolean","INTERSECT",EDGE,{"disambiguationData":[OD(0.0)],"derivedFrom":[makeQuery(id+"F3.opExtrude","SWEPT_FACE",FACE,{"disambiguationData":[OSD([sQuery(id+"F2.wireOp",EDGE,"E40.0")])]}),makeQuery(id+"F10.opExtrude","SWEPT_FACE",FACE,{"disambiguationData":[OSD([sQuery(id+"F9.wireOp",EDGE,"E44.left")])]})]});
            var Q61;
            {var subQ0=sQuery(id+"F5.wireOp",EDGE,"E42");var subQ1=sQuery(id+"F12.wireOp",EDGE,"E45.top");Q61=makeQuery(id+"F13.boolean.opBoolean","SPLIT",EDGE,{"disambiguationData":[TD([makeQuery(id+"F13.opExtrude","SWEPT_FACE",FACE,{"disambiguationData":[OSD([subQ1]),TDD([makeQuery(id+"F12.imprint","IMPRINT",EDGE,{"disambiguationData":[TD([[makeQuery(id+"F12.imprint","INTERSECT",VERTEX,{"derivedFrom":[subQ1,sQuery(id+"F12.wireOp",EDGE,"E45.left")]}),-1.0]])],"derivedFrom":subQ1})])]})])],"derivedFrom":makeQuery(id+"F7.opShell","OFFSET_EDGE",EDGE,{"disambiguationData":[OSD([subQ0]),TDD([makeQuery(id+"F6.boolean.opBoolean","COPY",EDGE,{"derivedFrom":makeQuery(id+"F6.opExtrude","CAP_EDGE",EDGE,{"disambiguationData":[OSD([subQ0])],"isStart":false})})])]})});}
            var Q62;
            {var subQ0=sQuery(id+"F12.wireOp",EDGE,"E46.left");Q62=makeQuery(id+"F13.boolean.opBoolean","INTERSECT",EDGE,{"derivedFrom":[makeQuery(id+"F7.opShell","OFFSET_FACE",FACE,{"disambiguationData":[OSD([sQuery(id+"F5.wireOp",EDGE,"E42"),sQuery(id+"F5.wireOp",EDGE,"E43")])]}),makeQuery(id+"F13.opExtrude","SWEPT_FACE",FACE,{"disambiguationData":[OSD([subQ0]),TDD([makeQuery(id+"F12.imprint","IMPRINT",EDGE,{"disambiguationData":[TD([[makeQuery(id+"F12.imprint","INTERSECT",VERTEX,{"derivedFrom":[sQuery(id+"F12.wireOp",EDGE,"E46.bottom"),subQ0]}),-1.0]])],"derivedFrom":subQ0})])]})]});}
            var Q63;
            {var subQ0=sQuery(id+"F12.wireOp",EDGE,"E46.right");var subQ1=sQuery(id+"F2.wireOp",EDGE,"E40.0");Q63=makeQuery(id+"F13.boolean.opBoolean","INTERSECT",EDGE,{"derivedFrom":[makeQuery(id+"F7.opShell","OFFSET_FACE",FACE,{"disambiguationData":[OSD([subQ1]),TDD([makeQuery(id+"F3.opExtrude","CAP_FACE",FACE,{"disambiguationData":[OSD([subQ1])],"isStart":true})])]}),makeQuery(id+"F13.opExtrude","SWEPT_FACE",FACE,{"disambiguationData":[OSD([subQ0]),TDD([makeQuery(id+"F12.imprint","IMPRINT",EDGE,{"disambiguationData":[TD([[makeQuery(id+"F12.imprint","INTERSECT",VERTEX,{"derivedFrom":[sQuery(id+"F12.wireOp",EDGE,"E46.top"),subQ0]}),1.0]])],"derivedFrom":subQ0})])]})]});}
            var Q64;
            {var subQ0=sQuery(id+"F12.wireOp",EDGE,"E45.bottom");var subQ1=sQuery(id+"F2.wireOp",EDGE,"E40.0");Q64=makeQuery(id+"F13.boolean.opBoolean","INTERSECT",EDGE,{"derivedFrom":[makeQuery(id+"F7.opShell","OFFSET_FACE",FACE,{"disambiguationData":[OSD([subQ1]),TDD([makeQuery(id+"F3.opExtrude","CAP_FACE",FACE,{"disambiguationData":[OSD([subQ1])],"isStart":true})])]}),makeQuery(id+"F13.opExtrude","SWEPT_FACE",FACE,{"disambiguationData":[OSD([subQ0]),TDD([makeQuery(id+"F12.imprint","IMPRINT",EDGE,{"disambiguationData":[TD([[makeQuery(id+"F12.imprint","INTERSECT",VERTEX,{"derivedFrom":[subQ0,sQuery(id+"F12.wireOp",EDGE,"E45.right")]}),1.0]])],"derivedFrom":subQ0})])]})]});}
            var Q65;
            {var subQ0=sQuery(id+"F12.wireOp",EDGE,"E45.bottom");Q65=makeQuery(id+"F13.boolean.opBoolean","INTERSECT",EDGE,{"derivedFrom":[makeQuery(id+"F7.opShell","OFFSET_FACE",FACE,{"disambiguationData":[OSD([sQuery(id+"F5.wireOp",EDGE,"E42"),sQuery(id+"F5.wireOp",EDGE,"E43")])]}),makeQuery(id+"F13.opExtrude","SWEPT_FACE",FACE,{"disambiguationData":[OSD([subQ0]),TDD([makeQuery(id+"F12.imprint","IMPRINT",EDGE,{"disambiguationData":[TD([[makeQuery(id+"F12.imprint","INTERSECT",VERTEX,{"derivedFrom":[subQ0,sQuery(id+"F12.wireOp",EDGE,"E45.right")]}),1.0]])],"derivedFrom":subQ0})])]})]});}
            var Q66;
            {var subQ0=sQuery(id+"F12.wireOp",EDGE,"E45.bottom");Q66=makeQuery(id+"F13.boolean.opBoolean","INTERSECT",EDGE,{"derivedFrom":[makeQuery(id+"F7.opShell","OFFSET_FACE",FACE,{"disambiguationData":[OSD([sQuery(id+"F5.wireOp",EDGE,"E42"),sQuery(id+"F5.wireOp",EDGE,"E43")])]}),makeQuery(id+"F13.opExtrude","SWEPT_FACE",FACE,{"disambiguationData":[OSD([subQ0]),TDD([makeQuery(id+"F12.imprint","IMPRINT",EDGE,{"disambiguationData":[TD([[makeQuery(id+"F12.imprint","INTERSECT",VERTEX,{"derivedFrom":[subQ0,sQuery(id+"F12.wireOp",EDGE,"E45.left")]}),-1.0]])],"derivedFrom":subQ0})])]})]});}
            var Q67;
            {var subQ0=sQuery(id+"F5.wireOp",EDGE,"E42");var subQ2=sQuery(id+"F12.wireOp",EDGE,"E45.bottom");Q67=makeQuery(id+"F13.boolean.opBoolean","SPLIT",EDGE,{"disambiguationData":[TD([makeQuery(id+"F13.opExtrude","SWEPT_FACE",FACE,{"disambiguationData":[OSD([subQ2]),TDD([makeQuery(id+"F12.imprint","IMPRINT",EDGE,{"disambiguationData":[TD([[makeQuery(id+"F12.imprint","INTERSECT",VERTEX,{"derivedFrom":[subQ2,sQuery(id+"F12.wireOp",EDGE,"E45.left")]}),-1.0]])],"derivedFrom":subQ2})])]})])],"derivedFrom":makeQuery(id+"F7.opShell","OFFSET_EDGE",EDGE,{"disambiguationData":[OSD([subQ0]),TDD([makeQuery(id+"F6.boolean.opBoolean","COPY",EDGE,{"derivedFrom":makeQuery(id+"F6.opExtrude","CAP_EDGE",EDGE,{"disambiguationData":[OSD([subQ0])],"isStart":true})})])]})});}
            var Q68;
            Q68=makeQuery(id+"F13.opExtrude","SWEPT_EDGE",EDGE,{"disambiguationData":[OSD([sQuery(id+"F12.wireOp",EDGE,"E45.bottom"),sQuery(id+"F12.wireOp",EDGE,"E46.right")])]});
            var Q69;
            {var subQ0=sQuery(id+"F12.wireOp",EDGE,"E46.left");Q69=makeQuery(id+"F13.boolean.opBoolean","INTERSECT",EDGE,{"derivedFrom":[makeQuery(id+"F7.opShell","OFFSET_FACE",FACE,{"disambiguationData":[OSD([sQuery(id+"F5.wireOp",EDGE,"E42"),sQuery(id+"F5.wireOp",EDGE,"E43")])]}),makeQuery(id+"F13.opExtrude","SWEPT_FACE",FACE,{"disambiguationData":[OSD([subQ0]),TDD([makeQuery(id+"F12.imprint","IMPRINT",EDGE,{"disambiguationData":[TD([[makeQuery(id+"F12.imprint","INTERSECT",VERTEX,{"derivedFrom":[sQuery(id+"F12.wireOp",EDGE,"E46.top"),subQ0]}),1.0]])],"derivedFrom":subQ0})])]})]});}
            var Q70;
            Q70=makeQuery(id+"F1.opExtrude","CAP_EDGE",EDGE,{"disambiguationData":[OSD([sQuery(id+"F0.wireOp",EDGE,"E1")])],"isStart":false});
            var Q71;
            {var subQ0=sQuery(id+"F12.wireOp",EDGE,"E45.top");var subQ1=sQuery(id+"F2.wireOp",EDGE,"E40.0");Q71=makeQuery(id+"F13.boolean.opBoolean","INTERSECT",EDGE,{"derivedFrom":[makeQuery(id+"F7.opShell","OFFSET_FACE",FACE,{"disambiguationData":[OSD([subQ1]),TDD([makeQuery(id+"F3.opExtrude","CAP_FACE",FACE,{"disambiguationData":[OSD([subQ1])],"isStart":true})])]}),makeQuery(id+"F13.opExtrude","SWEPT_FACE",FACE,{"disambiguationData":[OSD([subQ0]),TDD([makeQuery(id+"F12.imprint","IMPRINT",EDGE,{"disambiguationData":[TD([[makeQuery(id+"F12.imprint","INTERSECT",VERTEX,{"derivedFrom":[subQ0,sQuery(id+"F12.wireOp",EDGE,"E45.left")]}),-1.0]])],"derivedFrom":subQ0})])]})]});}
            var Q72;
            {var subQ0=sQuery(id+"F12.wireOp",EDGE,"E45.bottom");Q72=makeQuery(id+"F13.boolean.opBoolean","INTERSECT",EDGE,{"derivedFrom":[makeQuery(id+"F7.opShell","OFFSET_FACE",FACE,{"disambiguationData":[OSD([sQuery(id+"F5.wireOp",EDGE,"E42")])]}),makeQuery(id+"F13.opExtrude","SWEPT_FACE",FACE,{"disambiguationData":[OSD([subQ0]),TDD([makeQuery(id+"F12.imprint","IMPRINT",EDGE,{"disambiguationData":[TD([[makeQuery(id+"F12.imprint","INTERSECT",VERTEX,{"derivedFrom":[subQ0,sQuery(id+"F12.wireOp",EDGE,"E45.right")]}),1.0]])],"derivedFrom":subQ0})])]})]});}
            var Q73;
            Q73=makeQuery(id+"F1.opExtrude","SWEPT_EDGE",EDGE,{"disambiguationData":[OSD([sQuery(id+"F0.wireOp",EDGE,"E3.trimOffspring"),sQuery(id+"F0.wireOp",EDGE,"E26")])]});
            var Q74;
            Q74=makeQuery(id+"F1.opExtrude","SWEPT_EDGE",EDGE,{"disambiguationData":[OSD([sQuery(id+"F0.wireOp",EDGE,"E3.trimOffspring"),sQuery(id+"F0.wireOp",EDGE,"E27")])]});
            var Q75;
            {var subQ0=sQuery(id+"F12.wireOp",EDGE,"E46.left");var subQ1=sQuery(id+"F2.wireOp",EDGE,"E40.0");Q75=makeQuery(id+"F13.boolean.opBoolean","INTERSECT",EDGE,{"derivedFrom":[makeQuery(id+"F7.opShell","OFFSET_FACE",FACE,{"disambiguationData":[OSD([subQ1]),TDD([makeQuery(id+"F3.opExtrude","CAP_FACE",FACE,{"disambiguationData":[OSD([subQ1])],"isStart":true})])]}),makeQuery(id+"F13.opExtrude","SWEPT_FACE",FACE,{"disambiguationData":[OSD([subQ0]),TDD([makeQuery(id+"F12.imprint","IMPRINT",EDGE,{"disambiguationData":[TD([[makeQuery(id+"F12.imprint","INTERSECT",VERTEX,{"derivedFrom":[sQuery(id+"F12.wireOp",EDGE,"E46.bottom"),subQ0]}),-1.0]])],"derivedFrom":subQ0})])]})]});}
            var Q76;
            {var subQ0=sQuery(id+"F12.wireOp",EDGE,"E45.top");var subQ1=sQuery(id+"F2.wireOp",EDGE,"E40.0");Q76=makeQuery(id+"F13.boolean.opBoolean","INTERSECT",EDGE,{"derivedFrom":[makeQuery(id+"F7.opShell","OFFSET_FACE",FACE,{"disambiguationData":[OSD([subQ1]),TDD([makeQuery(id+"F3.opExtrude","CAP_FACE",FACE,{"disambiguationData":[OSD([subQ1])],"isStart":true})])]}),makeQuery(id+"F13.opExtrude","SWEPT_FACE",FACE,{"disambiguationData":[OSD([subQ0]),TDD([makeQuery(id+"F12.imprint","IMPRINT",EDGE,{"disambiguationData":[TD([[makeQuery(id+"F12.imprint","INTERSECT",VERTEX,{"derivedFrom":[subQ0,sQuery(id+"F12.wireOp",EDGE,"E45.right")]}),1.0]])],"derivedFrom":subQ0})])]})]});}
            var Q77;
            {var subQ0=sQuery(id+"F12.wireOp",EDGE,"E45.top");Q77=makeQuery(id+"F13.boolean.opBoolean","INTERSECT",EDGE,{"derivedFrom":[makeQuery(id+"F7.opShell","OFFSET_FACE",FACE,{"disambiguationData":[OSD([sQuery(id+"F5.wireOp",EDGE,"E42")])]}),makeQuery(id+"F13.opExtrude","SWEPT_FACE",FACE,{"disambiguationData":[OSD([subQ0]),TDD([makeQuery(id+"F12.imprint","IMPRINT",EDGE,{"disambiguationData":[TD([[makeQuery(id+"F12.imprint","INTERSECT",VERTEX,{"derivedFrom":[subQ0,sQuery(id+"F12.wireOp",EDGE,"E45.right")]}),1.0]])],"derivedFrom":subQ0})])]})]});}
            var Q78;
            {var subQ0=sQuery(id+"F12.wireOp",EDGE,"E46.left");var subQ1=sQuery(id+"F2.wireOp",EDGE,"E40.0");Q78=makeQuery(id+"F13.boolean.opBoolean","INTERSECT",EDGE,{"derivedFrom":[makeQuery(id+"F7.opShell","OFFSET_FACE",FACE,{"disambiguationData":[OSD([subQ1]),TDD([makeQuery(id+"F3.opExtrude","CAP_FACE",FACE,{"disambiguationData":[OSD([subQ1])],"isStart":true})])]}),makeQuery(id+"F13.opExtrude","SWEPT_FACE",FACE,{"disambiguationData":[OSD([subQ0]),TDD([makeQuery(id+"F12.imprint","IMPRINT",EDGE,{"disambiguationData":[TD([[makeQuery(id+"F12.imprint","INTERSECT",VERTEX,{"derivedFrom":[sQuery(id+"F12.wireOp",EDGE,"E46.top"),subQ0]}),1.0]])],"derivedFrom":subQ0})])]})]});}
            var Q79;
            Q79=makeQuery(id+"F1.opExtrude","CAP_EDGE",EDGE,{"disambiguationData":[OSD([sQuery(id+"F0.wireOp",EDGE,"E1")])],"isStart":true});
            var Q80;
            Q80=makeQuery(id+"F1.opExtrude","CAP_EDGE",EDGE,{"disambiguationData":[OSD([sQuery(id+"F0.wireOp",EDGE,"E3.trimOffspring")])],"isStart":true});
            var Q81;
            {var subQ0=sQuery(id+"F12.wireOp",EDGE,"E46.right");var subQ1=sQuery(id+"F2.wireOp",EDGE,"E40.0");Q81=makeQuery(id+"F13.boolean.opBoolean","INTERSECT",EDGE,{"derivedFrom":[makeQuery(id+"F7.opShell","OFFSET_FACE",FACE,{"disambiguationData":[OSD([subQ1]),TDD([makeQuery(id+"F3.opExtrude","CAP_FACE",FACE,{"disambiguationData":[OSD([subQ1])],"isStart":true})])]}),makeQuery(id+"F13.opExtrude","SWEPT_FACE",FACE,{"disambiguationData":[OSD([subQ0]),TDD([makeQuery(id+"F12.imprint","IMPRINT",EDGE,{"disambiguationData":[TD([[makeQuery(id+"F12.imprint","INTERSECT",VERTEX,{"derivedFrom":[sQuery(id+"F12.wireOp",EDGE,"E46.bottom"),subQ0]}),-1.0]])],"derivedFrom":subQ0})])]})]});}
            var Q82;
            {var subQ0=sQuery(id+"F12.wireOp",EDGE,"E45.bottom");var subQ1=sQuery(id+"F2.wireOp",EDGE,"E40.0");Q82=makeQuery(id+"F13.boolean.opBoolean","INTERSECT",EDGE,{"derivedFrom":[makeQuery(id+"F7.opShell","OFFSET_FACE",FACE,{"disambiguationData":[OSD([subQ1]),TDD([makeQuery(id+"F3.opExtrude","CAP_FACE",FACE,{"disambiguationData":[OSD([subQ1])],"isStart":true})])]}),makeQuery(id+"F13.opExtrude","SWEPT_FACE",FACE,{"disambiguationData":[OSD([subQ0]),TDD([makeQuery(id+"F12.imprint","IMPRINT",EDGE,{"disambiguationData":[TD([[makeQuery(id+"F12.imprint","INTERSECT",VERTEX,{"derivedFrom":[subQ0,sQuery(id+"F12.wireOp",EDGE,"E45.left")]}),-1.0]])],"derivedFrom":subQ0})])]})]});}
            var Q83;
            {var subQ0=sQuery(id+"F5.wireOp",EDGE,"E42");var subQ1=sQuery(id+"F12.wireOp",EDGE,"E45.bottom");Q83=makeQuery(id+"F13.boolean.opBoolean","SPLIT",EDGE,{"disambiguationData":[TD([makeQuery(id+"F13.opExtrude","SWEPT_FACE",FACE,{"disambiguationData":[OSD([subQ1]),TDD([makeQuery(id+"F12.imprint","IMPRINT",EDGE,{"disambiguationData":[TD([[makeQuery(id+"F12.imprint","INTERSECT",VERTEX,{"derivedFrom":[subQ1,sQuery(id+"F12.wireOp",EDGE,"E45.left")]}),-1.0]])],"derivedFrom":subQ1})])]})])],"derivedFrom":makeQuery(id+"F7.opShell","OFFSET_EDGE",EDGE,{"disambiguationData":[OSD([subQ0]),TDD([makeQuery(id+"F6.boolean.opBoolean","COPY",EDGE,{"derivedFrom":makeQuery(id+"F6.opExtrude","CAP_EDGE",EDGE,{"disambiguationData":[OSD([subQ0])],"isStart":false})})])]})});}
            var Q84;
            {var subQ0=sQuery(id+"F12.wireOp",EDGE,"E46.right");Q84=makeQuery(id+"F13.boolean.opBoolean","INTERSECT",EDGE,{"derivedFrom":[makeQuery(id+"F7.opShell","OFFSET_FACE",FACE,{"disambiguationData":[OSD([sQuery(id+"F5.wireOp",EDGE,"E42")])]}),makeQuery(id+"F13.opExtrude","SWEPT_FACE",FACE,{"disambiguationData":[OSD([subQ0]),TDD([makeQuery(id+"F12.imprint","IMPRINT",EDGE,{"disambiguationData":[TD([[makeQuery(id+"F12.imprint","INTERSECT",VERTEX,{"derivedFrom":[sQuery(id+"F12.wireOp",EDGE,"E46.bottom"),subQ0]}),-1.0]])],"derivedFrom":subQ0})])]})]});}
            var Q85;
            {var subQ0=sQuery(id+"F5.wireOp",EDGE,"E42");var subQ1=sQuery(id+"F12.wireOp",EDGE,"E45.bottom");Q85=makeQuery(id+"F13.boolean.opBoolean","SPLIT",EDGE,{"disambiguationData":[TD([makeQuery(id+"F13.opExtrude","SWEPT_FACE",FACE,{"disambiguationData":[OSD([subQ1]),TDD([makeQuery(id+"F12.imprint","IMPRINT",EDGE,{"disambiguationData":[TD([[makeQuery(id+"F12.imprint","INTERSECT",VERTEX,{"derivedFrom":[subQ1,sQuery(id+"F12.wireOp",EDGE,"E45.right")]}),1.0]])],"derivedFrom":subQ1})])]})])],"derivedFrom":makeQuery(id+"F7.opShell","OFFSET_EDGE",EDGE,{"disambiguationData":[OSD([subQ0]),TDD([makeQuery(id+"F6.boolean.opBoolean","COPY",EDGE,{"derivedFrom":makeQuery(id+"F6.opExtrude","CAP_EDGE",EDGE,{"disambiguationData":[OSD([subQ0])],"isStart":false})})])]})});}
            var Q86;
            Q86=makeQuery(id+"F1.opExtrude","CAP_EDGE",EDGE,{"disambiguationData":[OSD([sQuery(id+"F0.wireOp",EDGE,"E3.trimOffspring")])],"isStart":false});
            var Q87;
            {var subQ0=sQuery(id+"F12.wireOp",EDGE,"E46.right");Q87=makeQuery(id+"F13.boolean.opBoolean","INTERSECT",EDGE,{"derivedFrom":[makeQuery(id+"F7.opShell","OFFSET_FACE",FACE,{"disambiguationData":[OSD([sQuery(id+"F5.wireOp",EDGE,"E42")])]}),makeQuery(id+"F13.opExtrude","SWEPT_FACE",FACE,{"disambiguationData":[OSD([subQ0]),TDD([makeQuery(id+"F12.imprint","IMPRINT",EDGE,{"disambiguationData":[TD([[makeQuery(id+"F12.imprint","INTERSECT",VERTEX,{"derivedFrom":[sQuery(id+"F12.wireOp",EDGE,"E46.top"),subQ0]}),1.0]])],"derivedFrom":subQ0})])]})]});}
            var Q88;
            {var subQ0=sQuery(id+"F12.wireOp",EDGE,"E45.bottom");Q88=makeQuery(id+"F13.boolean.opBoolean","INTERSECT",EDGE,{"derivedFrom":[makeQuery(id+"F7.opShell","OFFSET_FACE",FACE,{"disambiguationData":[OSD([sQuery(id+"F5.wireOp",EDGE,"E42")])]}),makeQuery(id+"F13.opExtrude","SWEPT_FACE",FACE,{"disambiguationData":[OSD([subQ0]),TDD([makeQuery(id+"F12.imprint","IMPRINT",EDGE,{"disambiguationData":[TD([[makeQuery(id+"F12.imprint","INTERSECT",VERTEX,{"derivedFrom":[subQ0,sQuery(id+"F12.wireOp",EDGE,"E45.left")]}),-1.0]])],"derivedFrom":subQ0})])]})]});}
            var Q89;
            Q89=makeQuery(id+"F13.opExtrude","SWEPT_EDGE",EDGE,{"disambiguationData":[OSD([sQuery(id+"F12.wireOp",EDGE,"E45.top"),sQuery(id+"F12.wireOp",EDGE,"E46.right")])]});
            var Q90;
            Q90=makeQuery(id+"F1.opExtrude","CAP_EDGE",EDGE,{"disambiguationData":[OSD([sQuery(id+"F0.wireOp",EDGE,"E4.filletArc")])],"isStart":true});
            var Q91;
            {var subQ0=sQuery(id+"F12.wireOp",EDGE,"E45.top");Q91=makeQuery(id+"F13.boolean.opBoolean","INTERSECT",EDGE,{"derivedFrom":[makeQuery(id+"F7.opShell","OFFSET_FACE",FACE,{"disambiguationData":[OSD([sQuery(id+"F5.wireOp",EDGE,"E42")])]}),makeQuery(id+"F13.opExtrude","SWEPT_FACE",FACE,{"disambiguationData":[OSD([subQ0]),TDD([makeQuery(id+"F12.imprint","IMPRINT",EDGE,{"disambiguationData":[TD([[makeQuery(id+"F12.imprint","INTERSECT",VERTEX,{"derivedFrom":[subQ0,sQuery(id+"F12.wireOp",EDGE,"E45.left")]}),-1.0]])],"derivedFrom":subQ0})])]})]});}
            var Q92;
            {var subQ0=sQuery(id+"F12.wireOp",EDGE,"E46.right");Q92=makeQuery(id+"F13.boolean.opBoolean","INTERSECT",EDGE,{"derivedFrom":[makeQuery(id+"F7.opShell","OFFSET_FACE",FACE,{"disambiguationData":[OSD([sQuery(id+"F5.wireOp",EDGE,"E42"),sQuery(id+"F5.wireOp",EDGE,"E43")])]}),makeQuery(id+"F13.opExtrude","SWEPT_FACE",FACE,{"disambiguationData":[OSD([subQ0]),TDD([makeQuery(id+"F12.imprint","IMPRINT",EDGE,{"disambiguationData":[TD([[makeQuery(id+"F12.imprint","INTERSECT",VERTEX,{"derivedFrom":[sQuery(id+"F12.wireOp",EDGE,"E46.top"),subQ0]}),1.0]])],"derivedFrom":subQ0})])]})]});}
            var Q93;
            {var subQ0=sQuery(id+"F12.wireOp",EDGE,"E46.right");Q93=makeQuery(id+"F13.boolean.opBoolean","INTERSECT",EDGE,{"derivedFrom":[makeQuery(id+"F7.opShell","OFFSET_FACE",FACE,{"disambiguationData":[OSD([sQuery(id+"F5.wireOp",EDGE,"E42"),sQuery(id+"F5.wireOp",EDGE,"E43")])]}),makeQuery(id+"F13.opExtrude","SWEPT_FACE",FACE,{"disambiguationData":[OSD([subQ0]),TDD([makeQuery(id+"F12.imprint","IMPRINT",EDGE,{"disambiguationData":[TD([[makeQuery(id+"F12.imprint","INTERSECT",VERTEX,{"derivedFrom":[sQuery(id+"F12.wireOp",EDGE,"E46.bottom"),subQ0]}),-1.0]])],"derivedFrom":subQ0})])]})]});}
            var Q94;
            Q94=makeQuery(id+"F13.opExtrude","SWEPT_EDGE",EDGE,{"disambiguationData":[OSD([sQuery(id+"F12.wireOp",EDGE,"E45.top"),sQuery(id+"F12.wireOp",EDGE,"E46.left")])]});
            var Q95;
            {var subQ0=sQuery(id+"F12.wireOp",EDGE,"E46.left");Q95=makeQuery(id+"F13.boolean.opBoolean","INTERSECT",EDGE,{"derivedFrom":[makeQuery(id+"F7.opShell","OFFSET_FACE",FACE,{"disambiguationData":[OSD([sQuery(id+"F5.wireOp",EDGE,"E42")])]}),makeQuery(id+"F13.opExtrude","SWEPT_FACE",FACE,{"disambiguationData":[OSD([subQ0]),TDD([makeQuery(id+"F12.imprint","IMPRINT",EDGE,{"disambiguationData":[TD([[makeQuery(id+"F12.imprint","INTERSECT",VERTEX,{"derivedFrom":[sQuery(id+"F12.wireOp",EDGE,"E46.top"),subQ0]}),1.0]])],"derivedFrom":subQ0})])]})]});}
            var Q96;
            {var subQ0=sQuery(id+"F5.wireOp",EDGE,"E42");var subQ1=sQuery(id+"F12.wireOp",EDGE,"E45.bottom");Q96=makeQuery(id+"F13.boolean.opBoolean","SPLIT",EDGE,{"disambiguationData":[TD([makeQuery(id+"F13.opExtrude","SWEPT_FACE",FACE,{"disambiguationData":[OSD([subQ1]),TDD([makeQuery(id+"F12.imprint","IMPRINT",EDGE,{"disambiguationData":[TD([[makeQuery(id+"F12.imprint","INTERSECT",VERTEX,{"derivedFrom":[subQ1,sQuery(id+"F12.wireOp",EDGE,"E45.right")]}),1.0]])],"derivedFrom":subQ1})])]})])],"derivedFrom":makeQuery(id+"F7.opShell","OFFSET_EDGE",EDGE,{"disambiguationData":[OSD([subQ0]),TDD([makeQuery(id+"F6.boolean.opBoolean","COPY",EDGE,{"derivedFrom":makeQuery(id+"F6.opExtrude","CAP_EDGE",EDGE,{"disambiguationData":[OSD([subQ0])],"isStart":true})})])]})});}
            var Q97;
            Q97=makeQuery(id+"F1.opExtrude","SWEPT_EDGE",EDGE,{"disambiguationData":[OSD([sQuery(id+"F0.wireOp",EDGE,"E1"),sQuery(id+"F0.wireOp",EDGE,"E25")])]});
            var Q98;
            Q98=makeQuery(id+"F1.opExtrude","CAP_EDGE",EDGE,{"disambiguationData":[OSD([sQuery(id+"F0.wireOp",EDGE,"E9")])],"isStart":false});
            var Q99;
            Q99=makeQuery(id+"F16.boolean.opBoolean","COPY",EDGE,{"derivedFrom":makeQuery(id+"F16.opExtrude","CAP_EDGE",EDGE,{"disambiguationData":[OSD([sQuery(id+"F15.wireOp",EDGE,"E58.MirrorCS"),sQuery(id+"F15.wireOp",EDGE,"E59.MirrorCS")])],"isStart":true})});
            var Q100;
            Q100=makeQuery(id+"F16.boolean.opBoolean","COPY",EDGE,{"derivedFrom":makeQuery(id+"F16.opExtrude","CAP_EDGE",EDGE,{"disambiguationData":[OSD([sQuery(id+"F15.wireOp",EDGE,"E61.MirrorCS"),sQuery(id+"F15.wireOp",EDGE,"E62.MirrorCS")])],"isStart":true})});
            var Q101;
            Q101=makeQuery(id+"F16.boolean.opBoolean","COPY",EDGE,{"derivedFrom":makeQuery(id+"F16.opExtrude","CAP_EDGE",EDGE,{"disambiguationData":[OSD([sQuery(id+"F15.wireOp",EDGE,"E48.filletArc"),sQuery(id+"F15.wireOp",EDGE,"E51.filletArc")])],"isStart":true})});
            var Q102;
            Q102=makeQuery(id+"F16.boolean.opBoolean","COPY",EDGE,{"derivedFrom":makeQuery(id+"F16.opExtrude","CAP_EDGE",EDGE,{"disambiguationData":[OSD([sQuery(id+"F15.wireOp",EDGE,"E49.filletArc"),sQuery(id+"F15.wireOp",EDGE,"E50.filletArc")])],"isStart":true})});
            var Q103;
            {var subQ0=sQuery(id+"F0.wireOp",EDGE,"E12.filletArc");var subQ1=sQuery(id+"F0.wireOp",EDGE,"E11");var subQ2=sQuery(id+"F0.wireOp",EDGE,"E10.trimOffspring");var subQ3=sQuery(id+"F0.wireOp",EDGE,"E9");var subQ4=sQuery(id+"F0.wireOp",EDGE,"E25");var subQ5=sQuery(id+"F0.wireOp",EDGE,"E4.filletArc");var subQ6=sQuery(id+"F0.wireOp",EDGE,"E20.MirrorCS");var subQ7=sQuery(id+"F0.wireOp",EDGE,"E0");var subQ8=sQuery(id+"F0.wireOp",EDGE,"E33.filletArc");var subQ9=sQuery(id+"F0.wireOp",EDGE,"E1");var subQ10=sQuery(id+"F0.wireOp",EDGE,"E34.filletArc");var subQ11=sQuery(id+"F0.wireOp",EDGE,"E38");var subQ12=sQuery(id+"F0.wireOp",EDGE,"E18.MirrorCS");var subQ13=sQuery(id+"F0.wireOp",EDGE,"E16.MirrorCS");var subQ14=sQuery(id+"F0.wireOp",EDGE,"E7");var subQ15=sQuery(id+"F0.wireOp",EDGE,"E2.trimOffspring");var subQ16=sQuery(id+"F0.wireOp",EDGE,"E3.trimOffspring");var subQ17=sQuery(id+"F0.wireOp",EDGE,"E26");var subQ18=sQuery(id+"F0.wireOp",EDGE,"E27");var subQ19=sQuery(id+"F0.wireOp",EDGE,"E28");Q103=makeQuery(id+"F16.boolean.opBoolean","INTERSECT",EDGE,{"derivedFrom":[makeQuery(id+"F3.boolean.opBoolean","SPLIT",FACE,{"disambiguationData":[TD([makeQuery(id+"F1.opExtrude","SWEPT_FACE",FACE,{"disambiguationData":[OSD([subQ9])]})])],"derivedFrom":makeQuery(id+"F1.opExtrude","CAP_FACE",FACE,{"disambiguationData":[OSD([subQ7,subQ9,subQ15,subQ16,subQ5,subQ14,subQ3,subQ2,subQ1,subQ0,sQuery(id+"F0.wireOp",EDGE,"E13.MirrorCS"),sQuery(id+"F0.wireOp",EDGE,"E14.MirrorCS"),sQuery(id+"F0.wireOp",EDGE,"E15.MirrorCS"),subQ13,sQuery(id+"F0.wireOp",EDGE,"E17.MirrorCS"),sQuery(id+"F0.wireOp",EDGE,"E19.MirrorCS"),subQ6,sQuery(id+"F0.wireOp",EDGE,"E23.MirrorCS"),subQ4,subQ17,subQ18,subQ19,sQuery(id+"F0.wireOp",EDGE,"E29.MirrorCS"),subQ12,sQuery(id+"F0.wireOp",EDGE,"E30.MirrorCS"),sQuery(id+"F0.wireOp",EDGE,"E31.MirrorCS"),sQuery(id+"F0.wireOp",EDGE,"E32.filletArc"),subQ8,subQ10,sQuery(id+"F0.wireOp",EDGE,"E36"),sQuery(id+"F0.wireOp",EDGE,"E37"),subQ11,sQuery(id+"F0.wireOp",EDGE,"E39.filletArc")])],"isStart":true})}),makeQuery(id+"F16.opExtrude","SWEPT_FACE",FACE,{"disambiguationData":[OSD([sQuery(id+"F15.wireOp",EDGE,"E48.filletArc"),sQuery(id+"F15.wireOp",EDGE,"E51.filletArc")])]})]});}
            var Q104;
            {var subQ0=sQuery(id+"F0.wireOp",EDGE,"E12.filletArc");var subQ1=sQuery(id+"F0.wireOp",EDGE,"E11");var subQ2=sQuery(id+"F0.wireOp",EDGE,"E10.trimOffspring");var subQ3=sQuery(id+"F0.wireOp",EDGE,"E9");var subQ4=sQuery(id+"F0.wireOp",EDGE,"E25");var subQ5=sQuery(id+"F0.wireOp",EDGE,"E4.filletArc");var subQ6=sQuery(id+"F0.wireOp",EDGE,"E20.MirrorCS");var subQ7=sQuery(id+"F0.wireOp",EDGE,"E0");var subQ8=sQuery(id+"F0.wireOp",EDGE,"E33.filletArc");var subQ9=sQuery(id+"F0.wireOp",EDGE,"E1");var subQ10=sQuery(id+"F0.wireOp",EDGE,"E34.filletArc");var subQ11=sQuery(id+"F0.wireOp",EDGE,"E38");var subQ12=sQuery(id+"F0.wireOp",EDGE,"E18.MirrorCS");var subQ13=sQuery(id+"F0.wireOp",EDGE,"E16.MirrorCS");var subQ14=sQuery(id+"F0.wireOp",EDGE,"E7");var subQ15=sQuery(id+"F0.wireOp",EDGE,"E2.trimOffspring");var subQ16=sQuery(id+"F0.wireOp",EDGE,"E3.trimOffspring");var subQ17=sQuery(id+"F0.wireOp",EDGE,"E26");var subQ18=sQuery(id+"F0.wireOp",EDGE,"E27");var subQ19=sQuery(id+"F0.wireOp",EDGE,"E28");Q104=makeQuery(id+"F16.boolean.opBoolean","INTERSECT",EDGE,{"derivedFrom":[makeQuery(id+"F3.boolean.opBoolean","SPLIT",FACE,{"disambiguationData":[TD([makeQuery(id+"F1.opExtrude","SWEPT_FACE",FACE,{"disambiguationData":[OSD([subQ9])]})])],"derivedFrom":makeQuery(id+"F1.opExtrude","CAP_FACE",FACE,{"disambiguationData":[OSD([subQ7,subQ9,subQ15,subQ16,subQ5,subQ14,subQ3,subQ2,subQ1,subQ0,sQuery(id+"F0.wireOp",EDGE,"E13.MirrorCS"),sQuery(id+"F0.wireOp",EDGE,"E14.MirrorCS"),sQuery(id+"F0.wireOp",EDGE,"E15.MirrorCS"),subQ13,sQuery(id+"F0.wireOp",EDGE,"E17.MirrorCS"),sQuery(id+"F0.wireOp",EDGE,"E19.MirrorCS"),subQ6,sQuery(id+"F0.wireOp",EDGE,"E23.MirrorCS"),subQ4,subQ17,subQ18,subQ19,sQuery(id+"F0.wireOp",EDGE,"E29.MirrorCS"),subQ12,sQuery(id+"F0.wireOp",EDGE,"E30.MirrorCS"),sQuery(id+"F0.wireOp",EDGE,"E31.MirrorCS"),sQuery(id+"F0.wireOp",EDGE,"E32.filletArc"),subQ8,subQ10,sQuery(id+"F0.wireOp",EDGE,"E36"),sQuery(id+"F0.wireOp",EDGE,"E37"),subQ11,sQuery(id+"F0.wireOp",EDGE,"E39.filletArc")])],"isStart":true})}),makeQuery(id+"F16.opExtrude","SWEPT_FACE",FACE,{"disambiguationData":[OSD([sQuery(id+"F15.wireOp",EDGE,"E49.filletArc"),sQuery(id+"F15.wireOp",EDGE,"E50.filletArc")])]})]});}
            var Q105;
            Q105=makeQuery(id+"F16.boolean.opBoolean","COPY",EDGE,{"derivedFrom":makeQuery(id+"F16.opExtrude","SWEPT_EDGE",EDGE,{"disambiguationData":[OSD([sQuery(id+"F15.wireOp",EDGE,"E47.top"),sQuery(id+"F15.wireOp",EDGE,"E50.filletArc")])]})});
            var Q106;
            Q106=makeQuery(id+"F16.boolean.opBoolean","COPY",EDGE,{"derivedFrom":makeQuery(id+"F16.opExtrude","SWEPT_EDGE",EDGE,{"disambiguationData":[OSD([sQuery(id+"F15.wireOp",EDGE,"E62.MirrorCS"),sQuery(id+"F15.wireOp",EDGE,"E64")])]})});
            var Q107;
            {var subQ0=sQuery(id+"F0.wireOp",EDGE,"E29.MirrorCS");var subQ1=sQuery(id+"F0.wireOp",EDGE,"E23.MirrorCS");var subQ2=sQuery(id+"F0.wireOp",EDGE,"E17.MirrorCS");var subQ3=sQuery(id+"F0.wireOp",EDGE,"E15.MirrorCS");var subQ4=sQuery(id+"F0.wireOp",EDGE,"E20.MirrorCS");var subQ5=sQuery(id+"F0.wireOp",EDGE,"E0");var subQ6=sQuery(id+"F0.wireOp",EDGE,"E14.MirrorCS");var subQ7=sQuery(id+"F0.wireOp",EDGE,"E19.MirrorCS");var subQ8=sQuery(id+"F0.wireOp",EDGE,"E38");var subQ9=sQuery(id+"F0.wireOp",EDGE,"E18.MirrorCS");var subQ10=sQuery(id+"F0.wireOp",EDGE,"E16.MirrorCS");var subQ11=sQuery(id+"F0.wireOp",EDGE,"E7");var subQ12=sQuery(id+"F0.wireOp",EDGE,"E2.trimOffspring");var subQ13=sQuery(id+"F0.wireOp",EDGE,"E36");var subQ14=sQuery(id+"F0.wireOp",EDGE,"E30.MirrorCS");var subQ15=sQuery(id+"F0.wireOp",EDGE,"E13.MirrorCS");var subQ16=sQuery(id+"F0.wireOp",EDGE,"E31.MirrorCS");var subQ17=sQuery(id+"F0.wireOp",EDGE,"E32.filletArc");var subQ18=sQuery(id+"F0.wireOp",EDGE,"E37");var subQ19=sQuery(id+"F0.wireOp",EDGE,"E39.filletArc");Q107=makeQuery(id+"F16.boolean.opBoolean","INTERSECT",EDGE,{"derivedFrom":[makeQuery(id+"F3.boolean.opBoolean","SPLIT",FACE,{"disambiguationData":[TD([makeQuery(id+"F1.opExtrude","SWEPT_FACE",FACE,{"disambiguationData":[OSD([subQ15])]})])],"derivedFrom":makeQuery(id+"F1.opExtrude","CAP_FACE",FACE,{"disambiguationData":[OSD([subQ5,sQuery(id+"F0.wireOp",EDGE,"E1"),subQ12,sQuery(id+"F0.wireOp",EDGE,"E3.trimOffspring"),sQuery(id+"F0.wireOp",EDGE,"E4.filletArc"),subQ11,sQuery(id+"F0.wireOp",EDGE,"E9"),sQuery(id+"F0.wireOp",EDGE,"E10.trimOffspring"),sQuery(id+"F0.wireOp",EDGE,"E11"),sQuery(id+"F0.wireOp",EDGE,"E12.filletArc"),subQ15,subQ6,subQ3,subQ10,subQ2,subQ7,subQ4,subQ1,sQuery(id+"F0.wireOp",EDGE,"E25"),sQuery(id+"F0.wireOp",EDGE,"E26"),sQuery(id+"F0.wireOp",EDGE,"E27"),sQuery(id+"F0.wireOp",EDGE,"E28"),subQ0,subQ9,subQ14,subQ16,subQ17,sQuery(id+"F0.wireOp",EDGE,"E33.filletArc"),sQuery(id+"F0.wireOp",EDGE,"E34.filletArc"),subQ13,subQ18,subQ8,subQ19])],"isStart":true})}),makeQuery(id+"F16.opExtrude","SWEPT_FACE",FACE,{"disambiguationData":[OSD([sQuery(id+"F15.wireOp",EDGE,"E58.MirrorCS"),sQuery(id+"F15.wireOp",EDGE,"E59.MirrorCS")])]})]});}
            var Q108;
            {var subQ0=sQuery(id+"F0.wireOp",EDGE,"E29.MirrorCS");var subQ1=sQuery(id+"F0.wireOp",EDGE,"E23.MirrorCS");var subQ2=sQuery(id+"F0.wireOp",EDGE,"E17.MirrorCS");var subQ3=sQuery(id+"F0.wireOp",EDGE,"E15.MirrorCS");var subQ4=sQuery(id+"F0.wireOp",EDGE,"E20.MirrorCS");var subQ5=sQuery(id+"F0.wireOp",EDGE,"E0");var subQ6=sQuery(id+"F0.wireOp",EDGE,"E14.MirrorCS");var subQ7=sQuery(id+"F0.wireOp",EDGE,"E19.MirrorCS");var subQ8=sQuery(id+"F0.wireOp",EDGE,"E38");var subQ9=sQuery(id+"F0.wireOp",EDGE,"E18.MirrorCS");var subQ10=sQuery(id+"F0.wireOp",EDGE,"E16.MirrorCS");var subQ11=sQuery(id+"F0.wireOp",EDGE,"E7");var subQ12=sQuery(id+"F0.wireOp",EDGE,"E2.trimOffspring");var subQ13=sQuery(id+"F0.wireOp",EDGE,"E36");var subQ14=sQuery(id+"F0.wireOp",EDGE,"E30.MirrorCS");var subQ15=sQuery(id+"F0.wireOp",EDGE,"E13.MirrorCS");var subQ16=sQuery(id+"F0.wireOp",EDGE,"E31.MirrorCS");var subQ17=sQuery(id+"F0.wireOp",EDGE,"E32.filletArc");var subQ18=sQuery(id+"F0.wireOp",EDGE,"E37");var subQ19=sQuery(id+"F0.wireOp",EDGE,"E39.filletArc");Q108=makeQuery(id+"F16.boolean.opBoolean","INTERSECT",EDGE,{"derivedFrom":[makeQuery(id+"F3.boolean.opBoolean","SPLIT",FACE,{"disambiguationData":[TD([makeQuery(id+"F1.opExtrude","SWEPT_FACE",FACE,{"disambiguationData":[OSD([subQ15])]})])],"derivedFrom":makeQuery(id+"F1.opExtrude","CAP_FACE",FACE,{"disambiguationData":[OSD([subQ5,sQuery(id+"F0.wireOp",EDGE,"E1"),subQ12,sQuery(id+"F0.wireOp",EDGE,"E3.trimOffspring"),sQuery(id+"F0.wireOp",EDGE,"E4.filletArc"),subQ11,sQuery(id+"F0.wireOp",EDGE,"E9"),sQuery(id+"F0.wireOp",EDGE,"E10.trimOffspring"),sQuery(id+"F0.wireOp",EDGE,"E11"),sQuery(id+"F0.wireOp",EDGE,"E12.filletArc"),subQ15,subQ6,subQ3,subQ10,subQ2,subQ7,subQ4,subQ1,sQuery(id+"F0.wireOp",EDGE,"E25"),sQuery(id+"F0.wireOp",EDGE,"E26"),sQuery(id+"F0.wireOp",EDGE,"E27"),sQuery(id+"F0.wireOp",EDGE,"E28"),subQ0,subQ9,subQ14,subQ16,subQ17,sQuery(id+"F0.wireOp",EDGE,"E33.filletArc"),sQuery(id+"F0.wireOp",EDGE,"E34.filletArc"),subQ13,subQ18,subQ8,subQ19])],"isStart":true})}),makeQuery(id+"F16.opExtrude","SWEPT_FACE",FACE,{"disambiguationData":[OSD([sQuery(id+"F15.wireOp",EDGE,"E61.MirrorCS"),sQuery(id+"F15.wireOp",EDGE,"E62.MirrorCS")])]})]});}
            var Q109;
            {var subQ0=sQuery(id+"F0.wireOp",EDGE,"E29.MirrorCS");var subQ1=sQuery(id+"F0.wireOp",EDGE,"E23.MirrorCS");var subQ2=sQuery(id+"F0.wireOp",EDGE,"E17.MirrorCS");var subQ3=sQuery(id+"F0.wireOp",EDGE,"E15.MirrorCS");var subQ4=sQuery(id+"F0.wireOp",EDGE,"E20.MirrorCS");var subQ5=sQuery(id+"F0.wireOp",EDGE,"E0");var subQ6=sQuery(id+"F0.wireOp",EDGE,"E14.MirrorCS");var subQ7=sQuery(id+"F0.wireOp",EDGE,"E19.MirrorCS");var subQ8=sQuery(id+"F0.wireOp",EDGE,"E38");var subQ9=sQuery(id+"F0.wireOp",EDGE,"E18.MirrorCS");var subQ10=sQuery(id+"F0.wireOp",EDGE,"E16.MirrorCS");var subQ11=sQuery(id+"F0.wireOp",EDGE,"E7");var subQ12=sQuery(id+"F0.wireOp",EDGE,"E2.trimOffspring");var subQ13=sQuery(id+"F0.wireOp",EDGE,"E36");var subQ14=sQuery(id+"F0.wireOp",EDGE,"E30.MirrorCS");var subQ15=sQuery(id+"F0.wireOp",EDGE,"E13.MirrorCS");var subQ16=sQuery(id+"F0.wireOp",EDGE,"E31.MirrorCS");var subQ17=sQuery(id+"F0.wireOp",EDGE,"E32.filletArc");var subQ18=sQuery(id+"F0.wireOp",EDGE,"E37");var subQ19=sQuery(id+"F0.wireOp",EDGE,"E39.filletArc");Q109=makeQuery(id+"F16.boolean.opBoolean","INTERSECT",EDGE,{"derivedFrom":[makeQuery(id+"F3.boolean.opBoolean","SPLIT",FACE,{"disambiguationData":[TD([makeQuery(id+"F1.opExtrude","SWEPT_FACE",FACE,{"disambiguationData":[OSD([subQ15])]})])],"derivedFrom":makeQuery(id+"F1.opExtrude","CAP_FACE",FACE,{"disambiguationData":[OSD([subQ5,sQuery(id+"F0.wireOp",EDGE,"E1"),subQ12,sQuery(id+"F0.wireOp",EDGE,"E3.trimOffspring"),sQuery(id+"F0.wireOp",EDGE,"E4.filletArc"),subQ11,sQuery(id+"F0.wireOp",EDGE,"E9"),sQuery(id+"F0.wireOp",EDGE,"E10.trimOffspring"),sQuery(id+"F0.wireOp",EDGE,"E11"),sQuery(id+"F0.wireOp",EDGE,"E12.filletArc"),subQ15,subQ6,subQ3,subQ10,subQ2,subQ7,subQ4,subQ1,sQuery(id+"F0.wireOp",EDGE,"E25"),sQuery(id+"F0.wireOp",EDGE,"E26"),sQuery(id+"F0.wireOp",EDGE,"E27"),sQuery(id+"F0.wireOp",EDGE,"E28"),subQ0,subQ9,subQ14,subQ16,subQ17,sQuery(id+"F0.wireOp",EDGE,"E33.filletArc"),sQuery(id+"F0.wireOp",EDGE,"E34.filletArc"),subQ13,subQ18,subQ8,subQ19])],"isStart":true})}),makeQuery(id+"F16.opExtrude","SWEPT_FACE",FACE,{"disambiguationData":[OSD([sQuery(id+"F15.wireOp",EDGE,"E63")])]})]});}
            var Q110;
            {var subQ0=sQuery(id+"F0.wireOp",EDGE,"E29.MirrorCS");var subQ1=sQuery(id+"F0.wireOp",EDGE,"E23.MirrorCS");var subQ2=sQuery(id+"F0.wireOp",EDGE,"E17.MirrorCS");var subQ3=sQuery(id+"F0.wireOp",EDGE,"E15.MirrorCS");var subQ4=sQuery(id+"F0.wireOp",EDGE,"E20.MirrorCS");var subQ5=sQuery(id+"F0.wireOp",EDGE,"E0");var subQ6=sQuery(id+"F0.wireOp",EDGE,"E14.MirrorCS");var subQ7=sQuery(id+"F0.wireOp",EDGE,"E19.MirrorCS");var subQ8=sQuery(id+"F0.wireOp",EDGE,"E38");var subQ9=sQuery(id+"F0.wireOp",EDGE,"E18.MirrorCS");var subQ10=sQuery(id+"F0.wireOp",EDGE,"E16.MirrorCS");var subQ11=sQuery(id+"F0.wireOp",EDGE,"E7");var subQ12=sQuery(id+"F0.wireOp",EDGE,"E2.trimOffspring");var subQ13=sQuery(id+"F0.wireOp",EDGE,"E36");var subQ14=sQuery(id+"F0.wireOp",EDGE,"E30.MirrorCS");var subQ15=sQuery(id+"F0.wireOp",EDGE,"E13.MirrorCS");var subQ16=sQuery(id+"F0.wireOp",EDGE,"E31.MirrorCS");var subQ17=sQuery(id+"F0.wireOp",EDGE,"E32.filletArc");var subQ18=sQuery(id+"F0.wireOp",EDGE,"E37");var subQ19=sQuery(id+"F0.wireOp",EDGE,"E39.filletArc");Q110=makeQuery(id+"F16.boolean.opBoolean","INTERSECT",EDGE,{"derivedFrom":[makeQuery(id+"F3.boolean.opBoolean","SPLIT",FACE,{"disambiguationData":[TD([makeQuery(id+"F1.opExtrude","SWEPT_FACE",FACE,{"disambiguationData":[OSD([subQ15])]})])],"derivedFrom":makeQuery(id+"F1.opExtrude","CAP_FACE",FACE,{"disambiguationData":[OSD([subQ5,sQuery(id+"F0.wireOp",EDGE,"E1"),subQ12,sQuery(id+"F0.wireOp",EDGE,"E3.trimOffspring"),sQuery(id+"F0.wireOp",EDGE,"E4.filletArc"),subQ11,sQuery(id+"F0.wireOp",EDGE,"E9"),sQuery(id+"F0.wireOp",EDGE,"E10.trimOffspring"),sQuery(id+"F0.wireOp",EDGE,"E11"),sQuery(id+"F0.wireOp",EDGE,"E12.filletArc"),subQ15,subQ6,subQ3,subQ10,subQ2,subQ7,subQ4,subQ1,sQuery(id+"F0.wireOp",EDGE,"E25"),sQuery(id+"F0.wireOp",EDGE,"E26"),sQuery(id+"F0.wireOp",EDGE,"E27"),sQuery(id+"F0.wireOp",EDGE,"E28"),subQ0,subQ9,subQ14,subQ16,subQ17,sQuery(id+"F0.wireOp",EDGE,"E33.filletArc"),sQuery(id+"F0.wireOp",EDGE,"E34.filletArc"),subQ13,subQ18,subQ8,subQ19])],"isStart":true})}),makeQuery(id+"F16.opExtrude","SWEPT_FACE",FACE,{"disambiguationData":[OSD([sQuery(id+"F15.wireOp",EDGE,"E64")])]})]});}
            var Q111;
            {var subQ0=sQuery(id+"F0.wireOp",EDGE,"E12.filletArc");var subQ1=sQuery(id+"F0.wireOp",EDGE,"E11");var subQ2=sQuery(id+"F0.wireOp",EDGE,"E10.trimOffspring");var subQ3=sQuery(id+"F0.wireOp",EDGE,"E9");var subQ4=sQuery(id+"F0.wireOp",EDGE,"E25");var subQ5=sQuery(id+"F0.wireOp",EDGE,"E4.filletArc");var subQ6=sQuery(id+"F0.wireOp",EDGE,"E20.MirrorCS");var subQ7=sQuery(id+"F0.wireOp",EDGE,"E0");var subQ8=sQuery(id+"F0.wireOp",EDGE,"E33.filletArc");var subQ9=sQuery(id+"F0.wireOp",EDGE,"E1");var subQ10=sQuery(id+"F0.wireOp",EDGE,"E34.filletArc");var subQ11=sQuery(id+"F0.wireOp",EDGE,"E38");var subQ12=sQuery(id+"F0.wireOp",EDGE,"E18.MirrorCS");var subQ13=sQuery(id+"F0.wireOp",EDGE,"E16.MirrorCS");var subQ14=sQuery(id+"F0.wireOp",EDGE,"E7");var subQ15=sQuery(id+"F0.wireOp",EDGE,"E2.trimOffspring");var subQ16=sQuery(id+"F0.wireOp",EDGE,"E3.trimOffspring");var subQ17=sQuery(id+"F0.wireOp",EDGE,"E26");var subQ18=sQuery(id+"F0.wireOp",EDGE,"E27");var subQ19=sQuery(id+"F0.wireOp",EDGE,"E28");Q111=makeQuery(id+"F16.boolean.opBoolean","INTERSECT",EDGE,{"derivedFrom":[makeQuery(id+"F3.boolean.opBoolean","SPLIT",FACE,{"disambiguationData":[TD([makeQuery(id+"F1.opExtrude","SWEPT_FACE",FACE,{"disambiguationData":[OSD([subQ9])]})])],"derivedFrom":makeQuery(id+"F1.opExtrude","CAP_FACE",FACE,{"disambiguationData":[OSD([subQ7,subQ9,subQ15,subQ16,subQ5,subQ14,subQ3,subQ2,subQ1,subQ0,sQuery(id+"F0.wireOp",EDGE,"E13.MirrorCS"),sQuery(id+"F0.wireOp",EDGE,"E14.MirrorCS"),sQuery(id+"F0.wireOp",EDGE,"E15.MirrorCS"),subQ13,sQuery(id+"F0.wireOp",EDGE,"E17.MirrorCS"),sQuery(id+"F0.wireOp",EDGE,"E19.MirrorCS"),subQ6,sQuery(id+"F0.wireOp",EDGE,"E23.MirrorCS"),subQ4,subQ17,subQ18,subQ19,sQuery(id+"F0.wireOp",EDGE,"E29.MirrorCS"),subQ12,sQuery(id+"F0.wireOp",EDGE,"E30.MirrorCS"),sQuery(id+"F0.wireOp",EDGE,"E31.MirrorCS"),sQuery(id+"F0.wireOp",EDGE,"E32.filletArc"),subQ8,subQ10,sQuery(id+"F0.wireOp",EDGE,"E36"),sQuery(id+"F0.wireOp",EDGE,"E37"),subQ11,sQuery(id+"F0.wireOp",EDGE,"E39.filletArc")])],"isStart":true})}),makeQuery(id+"F16.opExtrude","SWEPT_FACE",FACE,{"disambiguationData":[OSD([sQuery(id+"F15.wireOp",EDGE,"E47.bottom")])]})]});}
            var Q112;
            {var subQ0=sQuery(id+"F0.wireOp",EDGE,"E12.filletArc");var subQ1=sQuery(id+"F0.wireOp",EDGE,"E11");var subQ2=sQuery(id+"F0.wireOp",EDGE,"E10.trimOffspring");var subQ3=sQuery(id+"F0.wireOp",EDGE,"E9");var subQ4=sQuery(id+"F0.wireOp",EDGE,"E25");var subQ5=sQuery(id+"F0.wireOp",EDGE,"E4.filletArc");var subQ6=sQuery(id+"F0.wireOp",EDGE,"E20.MirrorCS");var subQ7=sQuery(id+"F0.wireOp",EDGE,"E0");var subQ8=sQuery(id+"F0.wireOp",EDGE,"E33.filletArc");var subQ9=sQuery(id+"F0.wireOp",EDGE,"E1");var subQ10=sQuery(id+"F0.wireOp",EDGE,"E34.filletArc");var subQ11=sQuery(id+"F0.wireOp",EDGE,"E38");var subQ12=sQuery(id+"F0.wireOp",EDGE,"E18.MirrorCS");var subQ13=sQuery(id+"F0.wireOp",EDGE,"E16.MirrorCS");var subQ14=sQuery(id+"F0.wireOp",EDGE,"E7");var subQ15=sQuery(id+"F0.wireOp",EDGE,"E2.trimOffspring");var subQ16=sQuery(id+"F0.wireOp",EDGE,"E3.trimOffspring");var subQ17=sQuery(id+"F0.wireOp",EDGE,"E26");var subQ18=sQuery(id+"F0.wireOp",EDGE,"E27");var subQ19=sQuery(id+"F0.wireOp",EDGE,"E28");Q112=makeQuery(id+"F16.boolean.opBoolean","INTERSECT",EDGE,{"derivedFrom":[makeQuery(id+"F3.boolean.opBoolean","SPLIT",FACE,{"disambiguationData":[TD([makeQuery(id+"F1.opExtrude","SWEPT_FACE",FACE,{"disambiguationData":[OSD([subQ9])]})])],"derivedFrom":makeQuery(id+"F1.opExtrude","CAP_FACE",FACE,{"disambiguationData":[OSD([subQ7,subQ9,subQ15,subQ16,subQ5,subQ14,subQ3,subQ2,subQ1,subQ0,sQuery(id+"F0.wireOp",EDGE,"E13.MirrorCS"),sQuery(id+"F0.wireOp",EDGE,"E14.MirrorCS"),sQuery(id+"F0.wireOp",EDGE,"E15.MirrorCS"),subQ13,sQuery(id+"F0.wireOp",EDGE,"E17.MirrorCS"),sQuery(id+"F0.wireOp",EDGE,"E19.MirrorCS"),subQ6,sQuery(id+"F0.wireOp",EDGE,"E23.MirrorCS"),subQ4,subQ17,subQ18,subQ19,sQuery(id+"F0.wireOp",EDGE,"E29.MirrorCS"),subQ12,sQuery(id+"F0.wireOp",EDGE,"E30.MirrorCS"),sQuery(id+"F0.wireOp",EDGE,"E31.MirrorCS"),sQuery(id+"F0.wireOp",EDGE,"E32.filletArc"),subQ8,subQ10,sQuery(id+"F0.wireOp",EDGE,"E36"),sQuery(id+"F0.wireOp",EDGE,"E37"),subQ11,sQuery(id+"F0.wireOp",EDGE,"E39.filletArc")])],"isStart":true})}),makeQuery(id+"F16.opExtrude","SWEPT_FACE",FACE,{"disambiguationData":[OSD([sQuery(id+"F15.wireOp",EDGE,"E47.top")])]})]});}
            var Q113;
            Q113=makeQuery(id+"F16.boolean.opBoolean","COPY",EDGE,{"derivedFrom":makeQuery(id+"F16.opExtrude","SWEPT_EDGE",EDGE,{"disambiguationData":[OSD([sQuery(id+"F15.wireOp",EDGE,"E61.MirrorCS"),sQuery(id+"F15.wireOp",EDGE,"E63")])]})});
            var Q114;
            Q114=makeQuery(id+"F1.opExtrude","CAP_EDGE",EDGE,{"disambiguationData":[OSD([sQuery(id+"F0.wireOp",EDGE,"E9")])],"isStart":true});
            var Q115;
            Q115=makeQuery(id+"F16.boolean.opBoolean","COPY",EDGE,{"derivedFrom":makeQuery(id+"F16.opExtrude","SWEPT_EDGE",EDGE,{"disambiguationData":[OSD([sQuery(id+"F15.wireOp",EDGE,"E59.MirrorCS"),sQuery(id+"F15.wireOp",EDGE,"E63")])]})});
            var Q116;
            Q116=makeQuery(id+"F16.boolean.opBoolean","COPY",EDGE,{"derivedFrom":makeQuery(id+"F16.opExtrude","SWEPT_EDGE",EDGE,{"disambiguationData":[OSD([sQuery(id+"F15.wireOp",EDGE,"E47.bottom"),sQuery(id+"F15.wireOp",EDGE,"E48.filletArc")])]})});
            var Q117;
            Q117=makeQuery(id+"F16.boolean.opBoolean","COPY",EDGE,{"derivedFrom":makeQuery(id+"F16.opExtrude","SWEPT_EDGE",EDGE,{"disambiguationData":[OSD([sQuery(id+"F15.wireOp",EDGE,"E47.bottom"),sQuery(id+"F15.wireOp",EDGE,"E49.filletArc")])]})});
            var Q118;
            Q118=makeQuery(id+"F16.boolean.opBoolean","COPY",EDGE,{"derivedFrom":makeQuery(id+"F16.opExtrude","SWEPT_EDGE",EDGE,{"disambiguationData":[OSD([sQuery(id+"F15.wireOp",EDGE,"E58.MirrorCS"),sQuery(id+"F15.wireOp",EDGE,"E64")])]})});
            var Q119;
            Q119=makeQuery(id+"F16.boolean.opBoolean","COPY",EDGE,{"derivedFrom":makeQuery(id+"F16.opExtrude","SWEPT_EDGE",EDGE,{"disambiguationData":[OSD([sQuery(id+"F15.wireOp",EDGE,"E47.top"),sQuery(id+"F15.wireOp",EDGE,"E51.filletArc")])]})});
            var Q120;
            Q120=makeQuery(id+"F1.opExtrude","CAP_EDGE",EDGE,{"disambiguationData":[OSD([sQuery(id+"F0.wireOp",EDGE,"E10.trimOffspring")])],"isStart":false});
            var Q121;
            Q121=makeQuery(id+"F1.opExtrude","CAP_EDGE",EDGE,{"disambiguationData":[OSD([sQuery(id+"F0.wireOp",EDGE,"E10.trimOffspring")])],"isStart":true});
            var Q122;
            Q122=makeQuery(id+"F1.opExtrude","CAP_EDGE",EDGE,{"disambiguationData":[OSD([sQuery(id+"F0.wireOp",EDGE,"E23.MirrorCS")])],"isStart":false});
            var Q123;
            Q123=makeQuery(id+"F1.opExtrude","CAP_EDGE",EDGE,{"disambiguationData":[OSD([sQuery(id+"F0.wireOp",EDGE,"E12.filletArc")])],"isStart":false});
            var Q124;
            {var subQ0=sQuery(id+"F0.wireOp",EDGE,"E20.MirrorCS");var subQ1=sQuery(id+"F0.wireOp",EDGE,"E12.filletArc");var subQ2=sQuery(id+"F0.wireOp",EDGE,"E0");Q124=makeQuery(id+"F3.boolean.opBoolean","SPLIT",EDGE,{"disambiguationData":[TD([makeQuery(id+"F1.opExtrude","SWEPT_FACE",FACE,{"disambiguationData":[OSD([subQ1])]})])],"derivedFrom":makeQuery(id+"F1.opExtrude","CAP_EDGE",EDGE,{"disambiguationData":[OSD([subQ2,subQ0])],"isStart":false})});}
            var Q125;
            {var subQ0=sQuery(id+"F0.wireOp",EDGE,"E23.MirrorCS");var subQ1=sQuery(id+"F0.wireOp",EDGE,"E20.MirrorCS");var subQ2=sQuery(id+"F0.wireOp",EDGE,"E0");Q125=makeQuery(id+"F3.boolean.opBoolean","SPLIT",EDGE,{"disambiguationData":[TD([makeQuery(id+"F1.opExtrude","SWEPT_FACE",FACE,{"disambiguationData":[OSD([subQ0])]})])],"derivedFrom":makeQuery(id+"F1.opExtrude","CAP_EDGE",EDGE,{"disambiguationData":[OSD([subQ2,subQ1])],"isStart":false})});}
            var Q126;
            Q126=makeQuery(id+"F1.opExtrude","SWEPT_EDGE",EDGE,{"disambiguationData":[OSD([sQuery(id+"F0.wireOp",EDGE,"E20.MirrorCS"),sQuery(id+"F0.wireOp",EDGE,"E23.MirrorCS")])]});
            var Q127;
            Q127=makeQuery(id+"F1.opExtrude","CAP_EDGE",EDGE,{"disambiguationData":[OSD([sQuery(id+"F0.wireOp",EDGE,"E13.MirrorCS")])],"isStart":false});
            var Q128;
            Q128=makeQuery(id+"F1.opExtrude","CAP_EDGE",EDGE,{"disambiguationData":[OSD([sQuery(id+"F0.wireOp",EDGE,"E14.MirrorCS")])],"isStart":false});
            var Q129;
            Q129=makeQuery(id+"F1.opExtrude","CAP_EDGE",EDGE,{"disambiguationData":[OSD([sQuery(id+"F0.wireOp",EDGE,"E17.MirrorCS")])],"isStart":false});
            var Q130;
            Q130=makeQuery(id+"F1.opExtrude","CAP_EDGE",EDGE,{"disambiguationData":[OSD([sQuery(id+"F0.wireOp",EDGE,"E11")])],"isStart":false});
            var Q131;
            Q131=makeQuery(id+"F1.opExtrude","CAP_EDGE",EDGE,{"disambiguationData":[OSD([sQuery(id+"F0.wireOp",EDGE,"E19.MirrorCS")])],"isStart":false});
            var Q132;
            Q132=makeQuery(id+"F1.opExtrude","CAP_EDGE",EDGE,{"disambiguationData":[OSD([sQuery(id+"F0.wireOp",EDGE,"E15.MirrorCS")])],"isStart":false});
            var Q133;
            Q133=makeQuery(id+"F1.opExtrude","CAP_EDGE",EDGE,{"disambiguationData":[OSD([sQuery(id+"F0.wireOp",EDGE,"E23.MirrorCS")])],"isStart":true});
            var Q134;
            Q134=makeQuery(id+"F1.opExtrude","SWEPT_EDGE",EDGE,{"disambiguationData":[OSD([sQuery(id+"F0.wireOp",EDGE,"E17.MirrorCS"),sQuery(id+"F0.wireOp",EDGE,"E23.MirrorCS")])]});
            var Q135;
            Q135=makeQuery(id+"F1.opExtrude","SWEPT_EDGE",EDGE,{"disambiguationData":[OSD([sQuery(id+"F0.wireOp",EDGE,"E13.MirrorCS"),sQuery(id+"F0.wireOp",EDGE,"E19.MirrorCS")])]});
            var Q136;
            Q136=makeQuery(id+"F1.opExtrude","SWEPT_EDGE",EDGE,{"disambiguationData":[OSD([sQuery(id+"F0.wireOp",EDGE,"E19.MirrorCS"),sQuery(id+"F0.wireOp",EDGE,"E31.MirrorCS")])]});
            var Q137;
            Q137=makeQuery(id+"F1.opExtrude","SWEPT_EDGE",EDGE,{"disambiguationData":[OSD([sQuery(id+"F0.wireOp",EDGE,"E13.MirrorCS"),sQuery(id+"F0.wireOp",EDGE,"E14.MirrorCS")])]});
            var Q138;
            Q138=makeQuery(id+"F1.opExtrude","SWEPT_EDGE",EDGE,{"disambiguationData":[OSD([sQuery(id+"F0.wireOp",EDGE,"E15.MirrorCS"),sQuery(id+"F0.wireOp",EDGE,"E17.MirrorCS")])]});
            var Q139;
            Q139=makeQuery(id+"F1.opExtrude","SWEPT_EDGE",EDGE,{"disambiguationData":[OSD([sQuery(id+"F0.wireOp",EDGE,"E14.MirrorCS"),sQuery(id+"F0.wireOp",EDGE,"E15.MirrorCS")])]});
            var Q140;
            Q140=makeQuery(id+"F1.opExtrude","CAP_EDGE",EDGE,{"disambiguationData":[OSD([sQuery(id+"F0.wireOp",EDGE,"E14.MirrorCS")])],"isStart":true});
            var Q141;
            {var subQ0=sQuery(id+"F0.wireOp",EDGE,"E20.MirrorCS");var subQ1=sQuery(id+"F0.wireOp",EDGE,"E12.filletArc");var subQ2=sQuery(id+"F0.wireOp",EDGE,"E0");Q141=makeQuery(id+"F3.boolean.opBoolean","SPLIT",EDGE,{"disambiguationData":[TD([makeQuery(id+"F1.opExtrude","SWEPT_FACE",FACE,{"disambiguationData":[OSD([subQ1])]})])],"derivedFrom":makeQuery(id+"F1.opExtrude","CAP_EDGE",EDGE,{"disambiguationData":[OSD([subQ2,subQ0])],"isStart":true})});}
            var Q142;
            Q142=makeQuery(id+"F1.opExtrude","CAP_EDGE",EDGE,{"disambiguationData":[OSD([sQuery(id+"F0.wireOp",EDGE,"E12.filletArc")])],"isStart":true});
            var Q143;
            Q143=makeQuery(id+"F1.opExtrude","SWEPT_EDGE",EDGE,{"disambiguationData":[OSD([sQuery(id+"F0.wireOp",EDGE,"E11"),sQuery(id+"F0.wireOp",EDGE,"E12.filletArc")])]});
            var Q144;
            Q144=makeQuery(id+"F1.opExtrude","CAP_EDGE",EDGE,{"disambiguationData":[OSD([sQuery(id+"F0.wireOp",EDGE,"E11")])],"isStart":true});
            var Q145;
            Q145=makeQuery(id+"F1.opExtrude","CAP_EDGE",EDGE,{"disambiguationData":[OSD([sQuery(id+"F0.wireOp",EDGE,"E17.MirrorCS")])],"isStart":true});
            var Q146;
            Q146=makeQuery(id+"F1.opExtrude","CAP_EDGE",EDGE,{"disambiguationData":[OSD([sQuery(id+"F0.wireOp",EDGE,"E19.MirrorCS")])],"isStart":true});
            var Q147;
            {var subQ0=sQuery(id+"F0.wireOp",EDGE,"E23.MirrorCS");var subQ1=sQuery(id+"F0.wireOp",EDGE,"E20.MirrorCS");var subQ2=sQuery(id+"F0.wireOp",EDGE,"E0");Q147=makeQuery(id+"F3.boolean.opBoolean","SPLIT",EDGE,{"disambiguationData":[TD([makeQuery(id+"F1.opExtrude","SWEPT_FACE",FACE,{"disambiguationData":[OSD([subQ0])]})])],"derivedFrom":makeQuery(id+"F1.opExtrude","CAP_EDGE",EDGE,{"disambiguationData":[OSD([subQ2,subQ1])],"isStart":true})});}
            var Q148;
            Q148=makeQuery(id+"F1.opExtrude","CAP_EDGE",EDGE,{"disambiguationData":[OSD([sQuery(id+"F0.wireOp",EDGE,"E13.MirrorCS")])],"isStart":true});
            var Q149;
            Q149=makeQuery(id+"F1.opExtrude","CAP_EDGE",EDGE,{"disambiguationData":[OSD([sQuery(id+"F0.wireOp",EDGE,"E15.MirrorCS")])],"isStart":true});
            var Q150;
            Q150=makeQuery(id+"F1.opExtrude","CAP_EDGE",EDGE,{"disambiguationData":[OSD([sQuery(id+"F0.wireOp",EDGE,"E25")])],"isStart":false});
            var Q151;
            Q151=makeQuery(id+"F1.opExtrude","CAP_EDGE",EDGE,{"disambiguationData":[OSD([sQuery(id+"F0.wireOp",EDGE,"E31.MirrorCS")])],"isStart":false});
            var Q152;
            Q152=makeQuery(id+"F1.opExtrude","CAP_EDGE",EDGE,{"disambiguationData":[OSD([sQuery(id+"F0.wireOp",EDGE,"E28")])],"isStart":false});
            var Q153;
            Q153=makeQuery(id+"F1.opExtrude","CAP_EDGE",EDGE,{"disambiguationData":[OSD([sQuery(id+"F0.wireOp",EDGE,"E27")])],"isStart":false});
            var Q154;
            Q154=makeQuery(id+"F1.opExtrude","CAP_EDGE",EDGE,{"disambiguationData":[OSD([sQuery(id+"F0.wireOp",EDGE,"E30.MirrorCS")])],"isStart":false});
            var Q155;
            Q155=makeQuery(id+"F1.opExtrude","CAP_EDGE",EDGE,{"disambiguationData":[OSD([sQuery(id+"F0.wireOp",EDGE,"E26")])],"isStart":false});
            var Q156;
            Q156=makeQuery(id+"F1.opExtrude","CAP_EDGE",EDGE,{"disambiguationData":[OSD([sQuery(id+"F0.wireOp",EDGE,"E27")])],"isStart":true});
            var Q157;
            Q157=makeQuery(id+"F1.opExtrude","CAP_EDGE",EDGE,{"disambiguationData":[OSD([sQuery(id+"F0.wireOp",EDGE,"E30.MirrorCS")])],"isStart":true});
            var Q158;
            Q158=makeQuery(id+"F1.opExtrude","CAP_EDGE",EDGE,{"disambiguationData":[OSD([sQuery(id+"F0.wireOp",EDGE,"E25")])],"isStart":true});
            var Q159;
            Q159=makeQuery(id+"F1.opExtrude","CAP_EDGE",EDGE,{"disambiguationData":[OSD([sQuery(id+"F0.wireOp",EDGE,"E26")])],"isStart":true});
            var Q160;
            Q160=makeQuery(id+"F1.opExtrude","SWEPT_EDGE",EDGE,{"disambiguationData":[OSD([sQuery(id+"F0.wireOp",EDGE,"E7"),sQuery(id+"F0.wireOp",EDGE,"E28")])]});
            var Q161;
            Q161=makeQuery(id+"F1.opExtrude","SWEPT_EDGE",EDGE,{"disambiguationData":[OSD([sQuery(id+"F0.wireOp",EDGE,"E27"),sQuery(id+"F0.wireOp",EDGE,"E33.filletArc")])]});
            var Q162;
            Q162=makeQuery(id+"F1.opExtrude","SWEPT_EDGE",EDGE,{"disambiguationData":[OSD([sQuery(id+"F0.wireOp",EDGE,"E28"),sQuery(id+"F0.wireOp",EDGE,"E33.filletArc")])]});
            var Q163;
            Q163=makeQuery(id+"F1.opExtrude","SWEPT_EDGE",EDGE,{"disambiguationData":[OSD([sQuery(id+"F0.wireOp",EDGE,"E29.MirrorCS"),sQuery(id+"F0.wireOp",EDGE,"E30.MirrorCS")])]});
            var Q164;
            Q164=makeQuery(id+"F1.opExtrude","SWEPT_EDGE",EDGE,{"disambiguationData":[OSD([sQuery(id+"F0.wireOp",EDGE,"E30.MirrorCS"),sQuery(id+"F0.wireOp",EDGE,"E32.filletArc")])]});
            var Q165;
            Q165=makeQuery(id+"F1.opExtrude","SWEPT_EDGE",EDGE,{"disambiguationData":[OSD([sQuery(id+"F0.wireOp",EDGE,"E31.MirrorCS"),sQuery(id+"F0.wireOp",EDGE,"E32.filletArc")])]});
            var Q166;
            Q166=makeQuery(id+"F1.opExtrude","CAP_EDGE",EDGE,{"disambiguationData":[OSD([sQuery(id+"F0.wireOp",EDGE,"E28")])],"isStart":true});
            var Q167;
            Q167=makeQuery(id+"F1.opExtrude","CAP_EDGE",EDGE,{"disambiguationData":[OSD([sQuery(id+"F0.wireOp",EDGE,"E29.MirrorCS")])],"isStart":false});
            var Q168;
            Q168=makeQuery(id+"F1.opExtrude","SWEPT_EDGE",EDGE,{"disambiguationData":[OSD([sQuery(id+"F0.wireOp",EDGE,"E25"),sQuery(id+"F0.wireOp",EDGE,"E34.filletArc")])]});
            var Q169;
            Q169=makeQuery(id+"F1.opExtrude","SWEPT_EDGE",EDGE,{"disambiguationData":[OSD([sQuery(id+"F0.wireOp",EDGE,"E26"),sQuery(id+"F0.wireOp",EDGE,"E34.filletArc")])]});
            var Q170;
            {var subQ0=sQuery(id+"F0.wireOp",EDGE,"E38");var subQ1=sQuery(id+"F0.wireOp",EDGE,"E18.MirrorCS");var subQ2=sQuery(id+"F0.wireOp",EDGE,"E28");var subQ3=sQuery(id+"F0.wireOp",EDGE,"E16.MirrorCS");var subQ4=sQuery(id+"F0.wireOp",EDGE,"E7");var subQ5=sQuery(id+"F0.wireOp",EDGE,"E2.trimOffspring");Q170=makeQuery(id+"F3.boolean.opBoolean","SPLIT",EDGE,{"disambiguationData":[TD([makeQuery(id+"F1.opExtrude","SWEPT_FACE",FACE,{"disambiguationData":[OSD([subQ2])]})])],"derivedFrom":makeQuery(id+"F1.opExtrude","CAP_EDGE",EDGE,{"disambiguationData":[OSD([subQ5,subQ4,subQ3,subQ1,subQ0])],"isStart":false})});}
            var Q171;
            Q171=makeQuery(id+"F1.opExtrude","CAP_EDGE",EDGE,{"disambiguationData":[OSD([sQuery(id+"F0.wireOp",EDGE,"E31.MirrorCS")])],"isStart":true});
            var Q172;
            Q172=makeQuery(id+"F1.opExtrude","CAP_EDGE",EDGE,{"disambiguationData":[OSD([sQuery(id+"F0.wireOp",EDGE,"E29.MirrorCS")])],"isStart":true});
            var Q173;
            Q173=makeQuery(id+"F1.opExtrude","SWEPT_EDGE",EDGE,{"disambiguationData":[OSD([sQuery(id+"F0.wireOp",EDGE,"E29.MirrorCS"),sQuery(id+"F0.wireOp",EDGE,"E36")])]});
            var Q174;
            {var subQ0=sQuery(id+"F0.wireOp",EDGE,"E38");var subQ1=sQuery(id+"F0.wireOp",EDGE,"E18.MirrorCS");var subQ2=sQuery(id+"F0.wireOp",EDGE,"E28");var subQ3=sQuery(id+"F0.wireOp",EDGE,"E16.MirrorCS");var subQ4=sQuery(id+"F0.wireOp",EDGE,"E7");var subQ5=sQuery(id+"F0.wireOp",EDGE,"E2.trimOffspring");Q174=makeQuery(id+"F3.boolean.opBoolean","SPLIT",EDGE,{"disambiguationData":[TD([makeQuery(id+"F1.opExtrude","SWEPT_FACE",FACE,{"disambiguationData":[OSD([subQ2])]})])],"derivedFrom":makeQuery(id+"F1.opExtrude","CAP_EDGE",EDGE,{"disambiguationData":[OSD([subQ5,subQ4,subQ3,subQ1,subQ0])],"isStart":true})});}
            var Q175;
            Q175=makeQuery(id+"F1.opExtrude","CAP_EDGE",EDGE,{"disambiguationData":[OSD([sQuery(id+"F0.wireOp",EDGE,"E39.filletArc")])],"isStart":false});
            var Q176;
            Q176=makeQuery(id+"F16.boolean.opBoolean","COPY",EDGE,{"derivedFrom":makeQuery(id+"F16.opExtrude","CAP_EDGE",EDGE,{"disambiguationData":[OSD([sQuery(id+"F15.wireOp",EDGE,"E63")])],"isStart":true})});
            var Q177;
            Q177=makeQuery(id+"F16.boolean.opBoolean","COPY",EDGE,{"derivedFrom":makeQuery(id+"F16.opExtrude","CAP_EDGE",EDGE,{"disambiguationData":[OSD([sQuery(id+"F15.wireOp",EDGE,"E64")])],"isStart":true})});
            var Q178;
            Q178=makeQuery(id+"F16.boolean.opBoolean","COPY",EDGE,{"derivedFrom":makeQuery(id+"F16.opExtrude","CAP_EDGE",EDGE,{"disambiguationData":[OSD([sQuery(id+"F15.wireOp",EDGE,"E47.bottom")])],"isStart":true})});
            var Q179;
            Q179=makeQuery(id+"F16.boolean.opBoolean","COPY",EDGE,{"derivedFrom":makeQuery(id+"F16.opExtrude","CAP_EDGE",EDGE,{"disambiguationData":[OSD([sQuery(id+"F15.wireOp",EDGE,"E47.top")])],"isStart":true})});
            var Q180;
            Q180=makeQuery(id+"F1.opExtrude","CAP_EDGE",EDGE,{"disambiguationData":[OSD([sQuery(id+"F0.wireOp",EDGE,"E34.filletArc")])],"isStart":false});
            var Q181;
            Q181=makeQuery(id+"F1.opExtrude","CAP_EDGE",EDGE,{"disambiguationData":[OSD([sQuery(id+"F0.wireOp",EDGE,"E36")])],"isStart":false});
            var Q182;
            Q182=makeQuery(id+"F1.opExtrude","CAP_EDGE",EDGE,{"disambiguationData":[OSD([sQuery(id+"F0.wireOp",EDGE,"E37")])],"isStart":true});
            var Q183;
            Q183=makeQuery(id+"F1.opExtrude","CAP_EDGE",EDGE,{"disambiguationData":[OSD([sQuery(id+"F0.wireOp",EDGE,"E37")])],"isStart":false});
            var Q184;
            Q184=makeQuery(id+"F1.opExtrude","CAP_EDGE",EDGE,{"disambiguationData":[OSD([sQuery(id+"F0.wireOp",EDGE,"E32.filletArc")])],"isStart":false});
            var Q185;
            Q185=makeQuery(id+"F1.opExtrude","CAP_EDGE",EDGE,{"disambiguationData":[OSD([sQuery(id+"F0.wireOp",EDGE,"E33.filletArc")])],"isStart":true});
            var Q186;
            Q186=makeQuery(id+"F1.opExtrude","CAP_EDGE",EDGE,{"disambiguationData":[OSD([sQuery(id+"F0.wireOp",EDGE,"E33.filletArc")])],"isStart":false});
            var Q187;
            Q187=makeQuery(id+"F1.opExtrude","CAP_EDGE",EDGE,{"disambiguationData":[OSD([sQuery(id+"F0.wireOp",EDGE,"E34.filletArc")])],"isStart":true});
            var Q188;
            {var subQ0=sQuery(id+"F5.wireOp",EDGE,"E43");var subQ1=sQuery(id+"F5.wireOp",EDGE,"E42");var subQ2=sQuery(id+"F2.wireOp",EDGE,"E40.0");var subQ3=sQuery(id+"F12.wireOp",EDGE,"E45.bottom");Q188=makeQuery(id+"F13.boolean.opBoolean","SPLIT",EDGE,{"disambiguationData":[TD([makeQuery(id+"F13.opExtrude","SWEPT_FACE",FACE,{"disambiguationData":[OSD([subQ3]),TDD([makeQuery(id+"F12.imprint","IMPRINT",EDGE,{"disambiguationData":[TD([[makeQuery(id+"F12.imprint","INTERSECT",VERTEX,{"derivedFrom":[subQ3,sQuery(id+"F12.wireOp",EDGE,"E45.right")]}),1.0]])],"derivedFrom":subQ3})])]})])],"derivedFrom":makeQuery(id+"F7.opShell","OFFSET_EDGE",EDGE,{"disambiguationData":[OSD([subQ2,subQ1,subQ0])]})});}
            var Q189;
            {var subQ0=sQuery(id+"F5.wireOp",EDGE,"E43");var subQ1=sQuery(id+"F5.wireOp",EDGE,"E42");var subQ2=sQuery(id+"F2.wireOp",EDGE,"E40.0");var subQ3=sQuery(id+"F12.wireOp",EDGE,"E46.left");Q189=makeQuery(id+"F13.boolean.opBoolean","SPLIT",EDGE,{"disambiguationData":[TD([makeQuery(id+"F13.opExtrude","SWEPT_FACE",FACE,{"disambiguationData":[OSD([subQ3]),TDD([makeQuery(id+"F12.imprint","IMPRINT",EDGE,{"disambiguationData":[TD([[makeQuery(id+"F12.imprint","INTERSECT",VERTEX,{"derivedFrom":[sQuery(id+"F12.wireOp",EDGE,"E46.bottom"),subQ3]}),-1.0]])],"derivedFrom":subQ3})])]})])],"derivedFrom":makeQuery(id+"F7.opShell","OFFSET_EDGE",EDGE,{"disambiguationData":[OSD([subQ2,subQ1,subQ0])]})});}
            var Q190;
            Q190=makeQuery(id+"F1.opExtrude","SWEPT_EDGE",EDGE,{"disambiguationData":[OSD([sQuery(id+"F0.wireOp",EDGE,"E37"),sQuery(id+"F0.wireOp",EDGE,"E38")])]});
            var Q191;
            Q191=makeQuery(id+"F1.opExtrude","CAP_EDGE",EDGE,{"disambiguationData":[OSD([sQuery(id+"F0.wireOp",EDGE,"E36")])],"isStart":true});
            var Q192;
            Q192=makeQuery(id+"F1.opExtrude","CAP_EDGE",EDGE,{"disambiguationData":[OSD([sQuery(id+"F0.wireOp",EDGE,"E39.filletArc")])],"isStart":true});
            var Q193;
            Q193=makeQuery(id+"F1.opExtrude","CAP_EDGE",EDGE,{"disambiguationData":[OSD([sQuery(id+"F0.wireOp",EDGE,"E32.filletArc")])],"isStart":true});
            var Q194;
            Q194=makeQuery(id+"F1.opExtrude","SWEPT_EDGE",EDGE,{"disambiguationData":[OSD([sQuery(id+"F0.wireOp",EDGE,"E36"),sQuery(id+"F0.wireOp",EDGE,"E39.filletArc")])]});
            var Q195;
            Q195=makeQuery(id+"F1.opExtrude","SWEPT_EDGE",EDGE,{"disambiguationData":[OSD([sQuery(id+"F0.wireOp",EDGE,"E37"),sQuery(id+"F0.wireOp",EDGE,"E39.filletArc")])]});
            var Q196;
            {var subQ0=makeQuery(id+"F10.opExtrude","SWEPT_FACE",FACE,{"disambiguationData":[OSD([sQuery(id+"F9.wireOp",EDGE,"E44.bottom")])]});var subQ1=sQuery(id+"F12.wireOp",EDGE,"E45.left");var subQ2=sQuery(id+"F12.wireOp",EDGE,"E45.bottom");Q196=makeQuery(id+"F13.boolean.opBoolean","SPLIT",EDGE,{"disambiguationData":[TD([makeQuery(id+"F10.boolean.opBoolean","COPY",FACE,{"disambiguationData":[OD(0.0)],"derivedFrom":subQ0})])],"derivedFrom":makeQuery(id+"F13.opExtrude","SWEPT_EDGE",EDGE,{"disambiguationData":[OSD([subQ2,subQ1])]})});}
            var Q197;
            {var subQ1=sQuery(id+"F12.wireOp",EDGE,"E45.left");var subQ2=sQuery(id+"F12.wireOp",EDGE,"E45.top");var subQ3=makeQuery(id+"F10.opExtrude","SWEPT_FACE",FACE,{"disambiguationData":[OSD([sQuery(id+"F9.wireOp",EDGE,"E44.bottom")])]});Q197=makeQuery(id+"F13.boolean.opBoolean","SPLIT",EDGE,{"disambiguationData":[TD([makeQuery(id+"F10.boolean.opBoolean","COPY",FACE,{"disambiguationData":[OD(0.0)],"derivedFrom":subQ3})])],"derivedFrom":makeQuery(id+"F13.opExtrude","SWEPT_EDGE",EDGE,{"disambiguationData":[OSD([subQ2,subQ1])]})});}
            var Q198;
            {var subQ0=sQuery(id+"F0.wireOp",EDGE,"E38");var subQ1=sQuery(id+"F0.wireOp",EDGE,"E37");var subQ2=sQuery(id+"F0.wireOp",EDGE,"E18.MirrorCS");var subQ3=sQuery(id+"F0.wireOp",EDGE,"E16.MirrorCS");var subQ4=sQuery(id+"F0.wireOp",EDGE,"E7");var subQ5=sQuery(id+"F0.wireOp",EDGE,"E2.trimOffspring");Q198=makeQuery(id+"F3.boolean.opBoolean","SPLIT",EDGE,{"disambiguationData":[TD([makeQuery(id+"F1.opExtrude","SWEPT_FACE",FACE,{"disambiguationData":[OSD([subQ1])]})])],"derivedFrom":makeQuery(id+"F1.opExtrude","CAP_EDGE",EDGE,{"disambiguationData":[OSD([subQ5,subQ4,subQ3,subQ2,subQ0])],"isStart":false})});}
            var Q199;
            Q199=makeQuery(id+"F13.opExtrude","CAP_EDGE",EDGE,{"disambiguationData":[OSD([sQuery(id+"F12.wireOp",EDGE,"E45.left")])],"isStart":true});
            var Q200;
            Q200=makeQuery(id+"F13.boolean.opBoolean","INTERSECT",EDGE,{"derivedFrom":[makeQuery(id+"F7.opShell","OFFSET_FACE",FACE,{"disambiguationData":[OSD([sQuery(id+"F5.wireOp",EDGE,"E42"),sQuery(id+"F5.wireOp",EDGE,"E43")])]}),makeQuery(id+"F13.opExtrude","SWEPT_FACE",FACE,{"disambiguationData":[OSD([sQuery(id+"F12.wireOp",EDGE,"E45.left")])]})]});
            var Q201;
            {var subQ0=sQuery(id+"F0.wireOp",EDGE,"E38");var subQ1=sQuery(id+"F0.wireOp",EDGE,"E37");var subQ2=sQuery(id+"F0.wireOp",EDGE,"E18.MirrorCS");var subQ3=sQuery(id+"F0.wireOp",EDGE,"E16.MirrorCS");var subQ4=sQuery(id+"F0.wireOp",EDGE,"E7");var subQ5=sQuery(id+"F0.wireOp",EDGE,"E2.trimOffspring");Q201=makeQuery(id+"F3.boolean.opBoolean","SPLIT",EDGE,{"disambiguationData":[TD([makeQuery(id+"F1.opExtrude","SWEPT_FACE",FACE,{"disambiguationData":[OSD([subQ1])]})])],"derivedFrom":makeQuery(id+"F1.opExtrude","CAP_EDGE",EDGE,{"disambiguationData":[OSD([subQ5,subQ4,subQ3,subQ2,subQ0])],"isStart":true})});}
            var Q202;
            {var subQ0=sQuery(id+"F5.wireOp",EDGE,"E43");var subQ1=sQuery(id+"F5.wireOp",EDGE,"E42");var subQ2=sQuery(id+"F2.wireOp",EDGE,"E40.0");var subQ3=sQuery(id+"F12.wireOp",EDGE,"E45.top");Q202=makeQuery(id+"F13.boolean.opBoolean","SPLIT",EDGE,{"disambiguationData":[TD([makeQuery(id+"F13.opExtrude","SWEPT_FACE",FACE,{"disambiguationData":[OSD([subQ3]),TDD([makeQuery(id+"F12.imprint","IMPRINT",EDGE,{"disambiguationData":[TD([[makeQuery(id+"F12.imprint","INTERSECT",VERTEX,{"derivedFrom":[subQ3,sQuery(id+"F12.wireOp",EDGE,"E45.right")]}),1.0]])],"derivedFrom":subQ3})])]})])],"derivedFrom":makeQuery(id+"F7.opShell","OFFSET_EDGE",EDGE,{"disambiguationData":[OSD([subQ2,subQ1,subQ0])]})});}
            fillet(context, id + "F17", {"entities" : qUnion([Q0, Q1, Q2, Q3, Q4, Q5, Q6, Q7, Q8, Q9, Q10, Q11, Q12, Q13, Q14, Q15, Q16, Q17, Q18, Q19, Q20, Q21, Q22, Q23, Q24, Q25, Q26, Q27, Q28, Q29, Q30, Q31, Q32, Q33, Q34, Q35, Q36, Q37, Q38, Q39, Q40, Q41, Q42, Q43, Q44, Q45, Q46, Q47, Q48, Q49, Q50, Q51, Q52, Q53, Q54, Q55, Q56, Q57, Q58, Q59, Q60, Q61, Q62, Q63, Q64, Q65, Q66, Q67, Q68, Q69, Q70, Q71, Q72, Q73, Q74, Q75, Q76, Q77, Q78, Q79, Q80, Q81, Q82, Q83, Q84, Q85, Q86, Q87, Q88, Q89, Q90, Q91, Q92, Q93, Q94, Q95, Q96, Q97, Q98, Q99, Q100, Q101, Q102, Q103, Q104, Q105, Q106, Q107, Q108, Q109, Q110, Q111, Q112, Q113, Q114, Q115, Q116, Q117, Q118, Q119, Q120, Q121, Q122, Q123, Q124, Q125, Q126, Q127, Q128, Q129, Q130, Q131, Q132, Q133, Q134, Q135, Q136, Q137, Q138, Q139, Q140, Q141, Q142, Q143, Q144, Q145, Q146, Q147, Q148, Q149, Q150, Q151, Q152, Q153, Q154, Q155, Q156, Q157, Q158, Q159, Q160, Q161, Q162, Q163, Q164, Q165, Q166, Q167, Q168, Q169, Q170, Q171, Q172, Q173, Q174, Q175, Q176, Q177, Q178, Q179, Q180, Q181, Q182, Q183, Q184, Q185, Q186, Q187, Q188, Q189, Q190, Q191, Q192, Q193, Q194, Q195, Q196, Q197, Q198, Q199, Q200, Q201, Q202]), "radius" : 0.5 * mm, "tangentPropagation" : true, "allowEdgeOverflow" : false});
        }
    });
